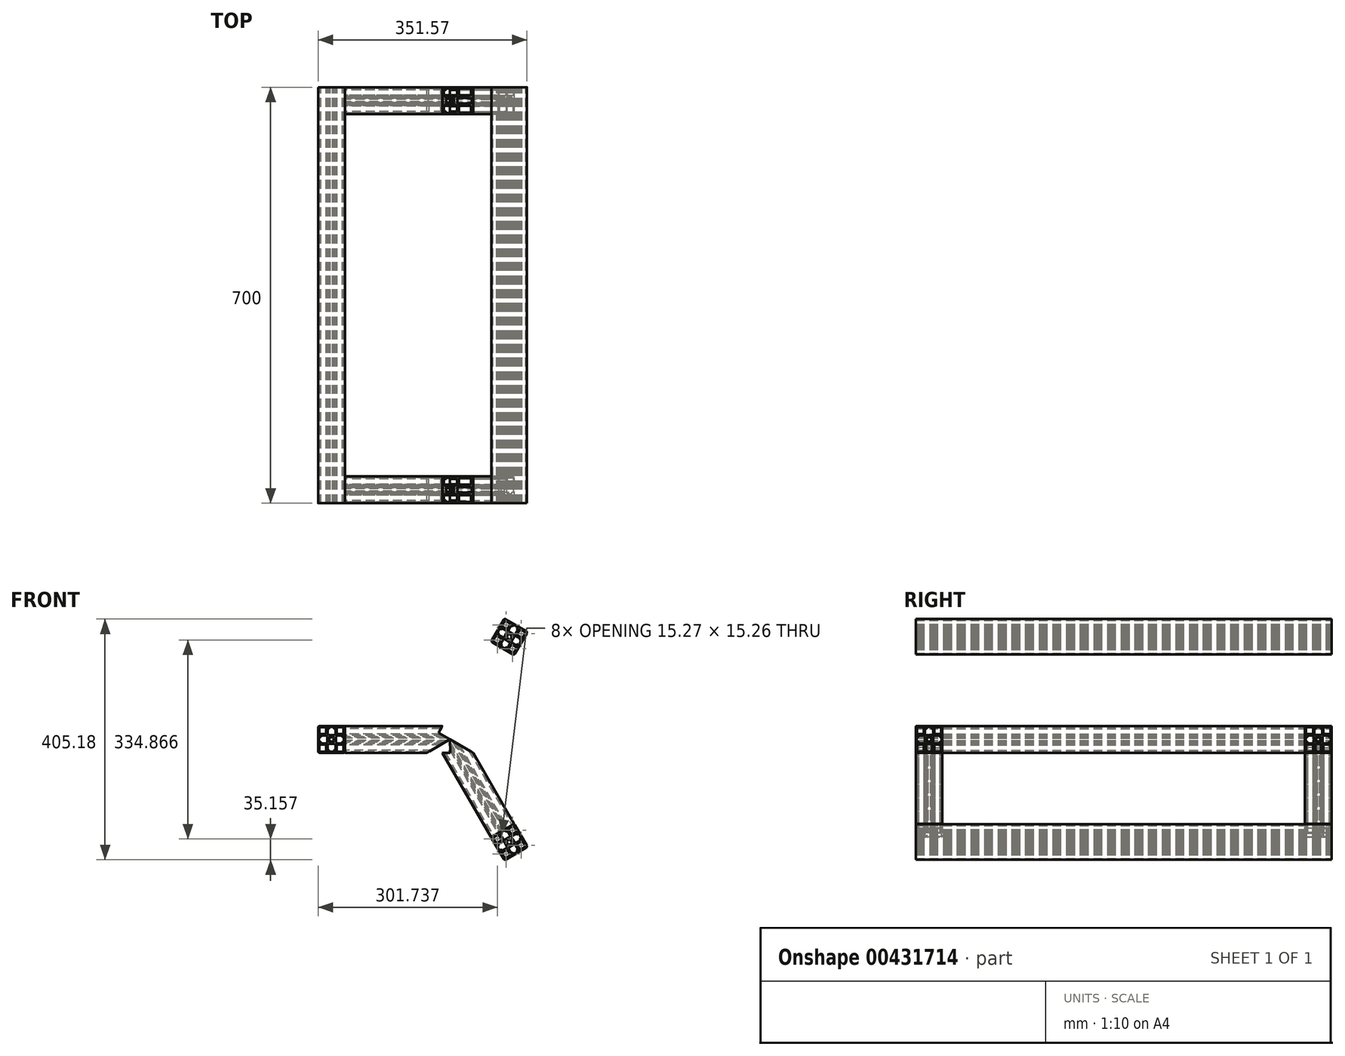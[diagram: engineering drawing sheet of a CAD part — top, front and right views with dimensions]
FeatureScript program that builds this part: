
annotation { "Feature Type Name" : "Feature", "Feature Type Description" : "" }
export const myFeature = defineFeature(function(context is Context, id is Id, definition is map)
    precondition{}
    {
        {
            var Q0;
            Q0=qCreatedBy(makeId("Front.planeOp"),FACE);
            var sketch = newSketch(context, id + "F0", { "sketchPlane" : qUnion([Q0])});
            skLineSegment(sketch, "E0", {"start": v(0, 22.5) * mm, "end": v(-20, 22.5) * mm});
            skLineSegment(sketch, "E1", {"start": v(-22.5, 20) * mm, "end": v(-22.5, 0) * mm});
            skLineSegment(sketch, "E2", {"start": v(0, 0) * mm, "end": v(-32.44, 0) * mm, "construction": true});
            skLineSegment(sketch, "E3", {"start": v(0, 0) * mm, "end": v(0, 27.63) * mm});
            skPoint(sketch, "E4.visualSharp", {"position": v(-22.5, 22.5) * mm});
            skArc(sketch, "E4.filletArc", {"start": v(-20, 22.5) * mm, "mid": v(-21.77, 21.77) * mm, "end": v(-22.5, 20) * mm});
            skLineSegment(sketch, "E5.bottom", {"start": v(-19.48, 8.8) * mm, "end": v(-9.78, 8.8) * mm});
            skLineSegment(sketch, "E5.top", {"start": v(-19.48, 20.52) * mm, "end": v(-9.78, 20.52) * mm});
            skLineSegment(sketch, "E5.left", {"start": v(-20.48, 9.8) * mm, "end": v(-20.48, 19.52) * mm});
            skLineSegment(sketch, "E5.right", {"start": v(-8.78, 9.8) * mm, "end": v(-8.78, 19.52) * mm});
            skLineSegment(sketch, "E6", {"start": v(-7.2, 0) * mm, "end": v(-7.2, 4.86) * mm});
            skLineSegment(sketch, "E7", {"start": v(-7.2, 4.86) * mm, "end": v(-9.19, 6.8) * mm});
            skLineSegment(sketch, "E8", {"start": v(-9.19, 6.8) * mm, "end": v(-18, 6.8) * mm});
            skLineSegment(sketch, "E9", {"start": v(-18, 6.8) * mm, "end": v(-18, 4.6) * mm});
            skLineSegment(sketch, "E10", {"start": v(-18.5, 4.1) * mm, "end": v(-22.2, 4.1) * mm});
            skLineSegment(sketch, "E11", {"start": v(-22.2, 4.1) * mm, "end": v(-22.2, 3.76) * mm});
            skLineSegment(sketch, "E12", {"start": v(-22.2, 3.76) * mm, "end": v(-21.67, 3.29) * mm});
            skLineSegment(sketch, "E13", {"start": v(-21, 1.8) * mm, "end": v(-21, 0) * mm});
            skLineSegment(sketch, "E14", {"start": v(0, 0) * mm, "end": v(-25.82, 25.82) * mm, "construction": true});
            skCircle(sketch, "E15", {"center": v(0, 0) * mm, "radius": 3.76 * mm});
            skLineSegment(sketch, "E16", {"start": v(-1.82, 3.3) * mm, "end": v(-3.13, 4.6) * mm});
            skLineSegment(sketch, "E17", {"start": v(-3.13, 4.6) * mm, "end": v(-3.86, 3.86) * mm});
            skPoint(sketch, "E18.visualSharp", {"position": v(-21, 2.7) * mm});
            skArc(sketch, "E18.filletArc", {"start": v(-21, 1.8) * mm, "mid": v(-21.17, 2.61) * mm, "end": v(-21.67, 3.29) * mm});
            skPoint(sketch, "E19.visualSharp", {"position": v(-18, 4.1) * mm});
            skArc(sketch, "E19.filletArc", {"start": v(-18.5, 4.1) * mm, "mid": v(-18.15, 4.24) * mm, "end": v(-18, 4.6) * mm});
            skPoint(sketch, "E20.visualSharp", {"position": v(-20.48, 20.52) * mm});
            skArc(sketch, "E20.filletArc", {"start": v(-19.48, 20.52) * mm, "mid": v(-20.19, 20.23) * mm, "end": v(-20.48, 19.52) * mm});
            skPoint(sketch, "E21.visualSharp", {"position": v(-20.48, 8.8) * mm});
            skArc(sketch, "E21.filletArc", {"start": v(-20.48, 9.8) * mm, "mid": v(-20.19, 9.1) * mm, "end": v(-19.48, 8.8) * mm});
            skPoint(sketch, "E22.visualSharp", {"position": v(-8.78, 8.8) * mm});
            skArc(sketch, "E22.filletArc", {"start": v(-9.78, 8.8) * mm, "mid": v(-9.07, 9.1) * mm, "end": v(-8.78, 9.8) * mm});
            skPoint(sketch, "E23.visualSharp", {"position": v(-8.78, 20.52) * mm});
            skArc(sketch, "E23.filletArc", {"start": v(-8.78, 19.52) * mm, "mid": v(-9.07, 20.23) * mm, "end": v(-9.78, 20.52) * mm});
            skLineSegment(sketch, "E24.MirrorCS", {"start": v(-4.86, 7.2) * mm, "end": v(-6.8, 9.19) * mm});
            skLineSegment(sketch, "E25.MirrorCS", {"start": v(0, 7.2) * mm, "end": v(-4.86, 7.2) * mm});
            skLineSegment(sketch, "E26.MirrorCS", {"start": v(-6.8, 9.19) * mm, "end": v(-6.8, 18) * mm});
            skLineSegment(sketch, "E27.MirrorCS", {"start": v(-6.8, 18) * mm, "end": v(-4.6, 18) * mm});
            skArc(sketch, "E28.MirrorCS", {"start": v(-4.1, 18.5) * mm, "mid": v(-4.24, 18.15) * mm, "end": v(-4.6, 18) * mm});
            skLineSegment(sketch, "E29.MirrorCS", {"start": v(-4.1, 18.5) * mm, "end": v(-4.1, 22.2) * mm});
            skLineSegment(sketch, "E30.MirrorCS", {"start": v(-1.8, 21) * mm, "end": v(0, 21) * mm});
            skArc(sketch, "E31.MirrorCS", {"start": v(-1.8, 21) * mm, "mid": v(-2.61, 21.17) * mm, "end": v(-3.29, 21.67) * mm});
            skLineSegment(sketch, "E32.MirrorCS", {"start": v(-3.76, 22.2) * mm, "end": v(-3.29, 21.67) * mm});
            skLineSegment(sketch, "E33.MirrorCS", {"start": v(-4.1, 22.2) * mm, "end": v(-3.76, 22.2) * mm});
            skLineSegment(sketch, "E34.MirrorCS", {"start": v(-3.3, 1.82) * mm, "end": v(-4.6, 3.13) * mm});
            skLineSegment(sketch, "E35.MirrorCS", {"start": v(-4.6, 3.13) * mm, "end": v(-3.86, 3.86) * mm});
            skLineSegment(sketch, "E36.MirrorCS", {"start": v(4.1, 22.2) * mm, "end": v(3.76, 22.2) * mm});
            skLineSegment(sketch, "E37.MirrorCS", {"start": v(3.76, 22.2) * mm, "end": v(3.29, 21.67) * mm});
            skLineSegment(sketch, "E38.MirrorCS", {"start": v(22.2, 3.76) * mm, "end": v(21.67, 3.29) * mm});
            skLineSegment(sketch, "E39.MirrorCS", {"start": v(22.2, 4.1) * mm, "end": v(22.2, 3.76) * mm});
            skArc(sketch, "E40.MirrorCS", {"start": v(4.1, 18.5) * mm, "mid": v(4.24, 18.15) * mm, "end": v(4.6, 18) * mm});
            skArc(sketch, "E41.MirrorCS", {"start": v(18.5, 4.1) * mm, "mid": v(18.15, 4.24) * mm, "end": v(18, 4.6) * mm});
            skArc(sketch, "E42.MirrorCS", {"start": v(19.48, 20.52) * mm, "mid": v(20.19, 20.23) * mm, "end": v(20.48, 19.52) * mm});
            skLineSegment(sketch, "E43.MirrorCS", {"start": v(3.13, 4.6) * mm, "end": v(3.86, 3.86) * mm});
            skLineSegment(sketch, "E44.MirrorCS", {"start": v(4.6, 3.13) * mm, "end": v(3.86, 3.86) * mm});
            skArc(sketch, "E45.MirrorCS", {"start": v(8.78, 19.52) * mm, "mid": v(9.07, 20.23) * mm, "end": v(9.78, 20.52) * mm});
            skArc(sketch, "E46.MirrorCS", {"start": v(9.78, 8.8) * mm, "mid": v(9.07, 9.1) * mm, "end": v(8.78, 9.8) * mm});
            skArc(sketch, "E47.MirrorCS", {"start": v(20.48, 9.8) * mm, "mid": v(20.19, 9.1) * mm, "end": v(19.48, 8.8) * mm});
            skArc(sketch, "E48.MirrorCS", {"start": v(21, 1.8) * mm, "mid": v(21.17, 2.61) * mm, "end": v(21.67, 3.29) * mm});
            skPoint(sketch, "E49.MirrorP", {"position": v(8.78, 8.8) * mm});
            skLineSegment(sketch, "E50.MirrorCS", {"start": v(4.86, 7.2) * mm, "end": v(6.8, 9.19) * mm});
            skLineSegment(sketch, "E51.MirrorCS", {"start": v(1.82, 3.3) * mm, "end": v(3.13, 4.6) * mm});
            skLineSegment(sketch, "E52.MirrorCS", {"start": v(6.8, 9.19) * mm, "end": v(6.8, 18) * mm});
            skLineSegment(sketch, "E53.MirrorCS", {"start": v(4.1, 18.5) * mm, "end": v(4.1, 22.2) * mm});
            skLineSegment(sketch, "E54.MirrorCS", {"start": v(21, 1.8) * mm, "end": v(21, 0) * mm});
            skPoint(sketch, "E55.MirrorP", {"position": v(20.48, 8.8) * mm});
            skPoint(sketch, "E56.MirrorP", {"position": v(20.48, 20.52) * mm});
            skPoint(sketch, "E57.MirrorP", {"position": v(8.78, 20.52) * mm});
            skLineSegment(sketch, "E58.MirrorCS", {"start": v(0, 0) * mm, "end": v(0, 27.63) * mm, "construction": true});
            skLineSegment(sketch, "E59.MirrorCS", {"start": v(22.5, 20) * mm, "end": v(22.5, 0) * mm});
            skLineSegment(sketch, "E60.MirrorCS", {"start": v(0, 22.5) * mm, "end": v(20, 22.5) * mm});
            skArc(sketch, "E61.MirrorCS", {"start": v(20, 22.5) * mm, "mid": v(21.77, 21.77) * mm, "end": v(22.5, 20) * mm});
            skLineSegment(sketch, "E62.MirrorCS", {"start": v(19.48, 8.8) * mm, "end": v(9.78, 8.8) * mm});
            skLineSegment(sketch, "E63.MirrorCS", {"start": v(19.48, 20.52) * mm, "end": v(9.78, 20.52) * mm});
            skLineSegment(sketch, "E64.MirrorCS", {"start": v(20.48, 9.8) * mm, "end": v(20.48, 19.52) * mm});
            skLineSegment(sketch, "E65.MirrorCS", {"start": v(8.78, 9.8) * mm, "end": v(8.78, 19.52) * mm});
            skLineSegment(sketch, "E66.MirrorCS", {"start": v(18.5, 4.1) * mm, "end": v(22.2, 4.1) * mm});
            skArc(sketch, "E67.MirrorCS", {"start": v(1.8, 21) * mm, "mid": v(2.61, 21.17) * mm, "end": v(3.29, 21.67) * mm});
            skLineSegment(sketch, "E68.MirrorCS", {"start": v(7.2, 0) * mm, "end": v(7.2, 4.86) * mm});
            skLineSegment(sketch, "E69.MirrorCS", {"start": v(7.2, 4.86) * mm, "end": v(9.19, 6.8) * mm});
            skPoint(sketch, "E70.MirrorP", {"position": v(21, 2.7) * mm});
            skLineSegment(sketch, "E71.MirrorCS", {"start": v(9.19, 6.8) * mm, "end": v(18, 6.8) * mm});
            skPoint(sketch, "E72.MirrorP", {"position": v(18, 4.1) * mm});
            skLineSegment(sketch, "E73.MirrorCS", {"start": v(3.3, 1.82) * mm, "end": v(4.6, 3.13) * mm});
            skLineSegment(sketch, "E74.MirrorCS", {"start": v(18, 6.8) * mm, "end": v(18, 4.6) * mm});
            skLineSegment(sketch, "E75.MirrorCS", {"start": v(1.8, 21) * mm, "end": v(0, 21) * mm});
            skLineSegment(sketch, "E76.MirrorCS", {"start": v(0, 7.2) * mm, "end": v(4.86, 7.2) * mm});
            skLineSegment(sketch, "E77.MirrorCS", {"start": v(6.8, 18) * mm, "end": v(4.6, 18) * mm});
            skPoint(sketch, "E78.MirrorP", {"position": v(22.5, 22.5) * mm});
            skArc(sketch, "E79.MirrorCS", {"start": v(18.5, -4.1) * mm, "mid": v(18.15, -4.24) * mm, "end": v(18, -4.6) * mm});
            skArc(sketch, "E80.MirrorCS", {"start": v(-18.5, -4.1) * mm, "mid": v(-18.15, -4.24) * mm, "end": v(-18, -4.6) * mm});
            skLineSegment(sketch, "E81.MirrorCS", {"start": v(-3.76, -22.2) * mm, "end": v(-3.29, -21.67) * mm});
            skLineSegment(sketch, "E82.MirrorCS", {"start": v(22.2, -4.1) * mm, "end": v(22.2, -3.76) * mm});
            skLineSegment(sketch, "E83.MirrorCS", {"start": v(22.2, -3.76) * mm, "end": v(21.67, -3.29) * mm});
            skLineSegment(sketch, "E84.MirrorCS", {"start": v(-22.2, -3.76) * mm, "end": v(-21.67, -3.29) * mm});
            skLineSegment(sketch, "E85.MirrorCS", {"start": v(-22.2, -4.1) * mm, "end": v(-22.2, -3.76) * mm});
            skArc(sketch, "E86.MirrorCS", {"start": v(4.1, -18.5) * mm, "mid": v(4.24, -18.15) * mm, "end": v(4.6, -18) * mm});
            skLineSegment(sketch, "E87.MirrorCS", {"start": v(4.1, -22.2) * mm, "end": v(3.76, -22.2) * mm});
            skLineSegment(sketch, "E88.MirrorCS", {"start": v(-4.1, -22.2) * mm, "end": v(-3.76, -22.2) * mm});
            skLineSegment(sketch, "E89.MirrorCS", {"start": v(3.76, -22.2) * mm, "end": v(3.29, -21.67) * mm});
            skArc(sketch, "E90.MirrorCS", {"start": v(-4.1, -18.5) * mm, "mid": v(-4.24, -18.15) * mm, "end": v(-4.6, -18) * mm});
            skArc(sketch, "E91.MirrorCS", {"start": v(-19.48, -20.52) * mm, "mid": v(-20.19, -20.23) * mm, "end": v(-20.48, -19.52) * mm});
            skArc(sketch, "E92.MirrorCS", {"start": v(19.48, -20.52) * mm, "mid": v(20.19, -20.23) * mm, "end": v(20.48, -19.52) * mm});
            skLineSegment(sketch, "E93.MirrorCS", {"start": v(3.13, -4.6) * mm, "end": v(3.86, -3.86) * mm});
            skArc(sketch, "E94.MirrorCS", {"start": v(21, -1.8) * mm, "mid": v(21.17, -2.61) * mm, "end": v(21.67, -3.29) * mm});
            skLineSegment(sketch, "E95.MirrorCS", {"start": v(-1.82, -3.3) * mm, "end": v(-3.13, -4.6) * mm});
            skArc(sketch, "E96.MirrorCS", {"start": v(-8.78, -19.52) * mm, "mid": v(-9.07, -20.23) * mm, "end": v(-9.78, -20.52) * mm});
            skArc(sketch, "E97.MirrorCS", {"start": v(20.48, -9.8) * mm, "mid": v(20.19, -9.1) * mm, "end": v(19.48, -8.8) * mm});
            skArc(sketch, "E98.MirrorCS", {"start": v(1.8, -21) * mm, "mid": v(2.61, -21.17) * mm, "end": v(3.29, -21.67) * mm});
            skArc(sketch, "E99.MirrorCS", {"start": v(-1.8, -21) * mm, "mid": v(-2.61, -21.17) * mm, "end": v(-3.29, -21.67) * mm});
            skArc(sketch, "E100.MirrorCS", {"start": v(-9.78, -8.8) * mm, "mid": v(-9.07, -9.1) * mm, "end": v(-8.78, -9.8) * mm});
            skArc(sketch, "E101.MirrorCS", {"start": v(9.78, -8.8) * mm, "mid": v(9.07, -9.1) * mm, "end": v(8.78, -9.8) * mm});
            skLineSegment(sketch, "E102.MirrorCS", {"start": v(-3.13, -4.6) * mm, "end": v(-3.86, -3.86) * mm});
            skArc(sketch, "E103.MirrorCS", {"start": v(8.78, -19.52) * mm, "mid": v(9.07, -20.23) * mm, "end": v(9.78, -20.52) * mm});
            skLineSegment(sketch, "E104.MirrorCS", {"start": v(-1.8, -21) * mm, "end": v(0, -21) * mm});
            skArc(sketch, "E105.MirrorCS", {"start": v(-20.48, -9.8) * mm, "mid": v(-20.19, -9.1) * mm, "end": v(-19.48, -8.8) * mm});
            skLineSegment(sketch, "E106.MirrorCS", {"start": v(1.82, -3.3) * mm, "end": v(3.13, -4.6) * mm});
            skArc(sketch, "E107.MirrorCS", {"start": v(-21, -1.8) * mm, "mid": v(-21.17, -2.61) * mm, "end": v(-21.67, -3.29) * mm});
            skLineSegment(sketch, "E108.MirrorCS", {"start": v(-3.3, -1.82) * mm, "end": v(-4.6, -3.13) * mm});
            skLineSegment(sketch, "E109.MirrorCS", {"start": v(1.8, -21) * mm, "end": v(0, -21) * mm});
            skLineSegment(sketch, "E110.MirrorCS", {"start": v(4.6, -3.13) * mm, "end": v(3.86, -3.86) * mm});
            skLineSegment(sketch, "E111.MirrorCS", {"start": v(-4.6, -3.13) * mm, "end": v(-3.86, -3.86) * mm});
            skLineSegment(sketch, "E112.MirrorCS", {"start": v(21, -1.8) * mm, "end": v(21, 0) * mm});
            skLineSegment(sketch, "E113.MirrorCS", {"start": v(3.3, -1.82) * mm, "end": v(4.6, -3.13) * mm});
            skLineSegment(sketch, "E114.MirrorCS", {"start": v(-21, -1.8) * mm, "end": v(-21, 0) * mm});
            skPoint(sketch, "E115.MirrorP", {"position": v(-20.48, -8.8) * mm});
            skPoint(sketch, "E116.MirrorP", {"position": v(22.5, -22.5) * mm});
            skPoint(sketch, "E117.MirrorP", {"position": v(20.48, -8.8) * mm});
            skPoint(sketch, "E118.MirrorP", {"position": v(-22.5, -22.5) * mm});
            skLineSegment(sketch, "E119.MirrorCS", {"start": v(7.2, 0) * mm, "end": v(7.2, -4.86) * mm});
            skLineSegment(sketch, "E120.MirrorCS", {"start": v(22.5, -20) * mm, "end": v(22.5, 0) * mm});
            skLineSegment(sketch, "E121.MirrorCS", {"start": v(6.8, -18) * mm, "end": v(4.6, -18) * mm});
            skPoint(sketch, "E122.MirrorP", {"position": v(18, -4.1) * mm});
            skPoint(sketch, "E123.MirrorP", {"position": v(-18, -4.1) * mm});
            skPoint(sketch, "E124.MirrorP", {"position": v(21, -2.7) * mm});
            skLineSegment(sketch, "E125.MirrorCS", {"start": v(-18, -6.8) * mm, "end": v(-18, -4.6) * mm});
            skLineSegment(sketch, "E126.MirrorCS", {"start": v(-9.19, -6.8) * mm, "end": v(-18, -6.8) * mm});
            skLineSegment(sketch, "E127.MirrorCS", {"start": v(0, -7.2) * mm, "end": v(4.86, -7.2) * mm});
            skLineSegment(sketch, "E128.MirrorCS", {"start": v(-7.2, -4.86) * mm, "end": v(-9.19, -6.8) * mm});
            skLineSegment(sketch, "E129.MirrorCS", {"start": v(-7.2, 0) * mm, "end": v(-7.2, -4.86) * mm});
            skLineSegment(sketch, "E130.MirrorCS", {"start": v(-8.78, -9.8) * mm, "end": v(-8.78, -19.52) * mm});
            skLineSegment(sketch, "E131.MirrorCS", {"start": v(-20.48, -9.8) * mm, "end": v(-20.48, -19.52) * mm});
            skLineSegment(sketch, "E132.MirrorCS", {"start": v(-19.48, -20.52) * mm, "end": v(-9.78, -20.52) * mm});
            skLineSegment(sketch, "E133.MirrorCS", {"start": v(-19.48, -8.8) * mm, "end": v(-9.78, -8.8) * mm});
            skArc(sketch, "E134.MirrorCS", {"start": v(-20, -22.5) * mm, "mid": v(-21.77, -21.77) * mm, "end": v(-22.5, -20) * mm});
            skLineSegment(sketch, "E135.MirrorCS", {"start": v(-22.5, -20) * mm, "end": v(-22.5, 0) * mm});
            skLineSegment(sketch, "E136.MirrorCS", {"start": v(0, -22.5) * mm, "end": v(-20, -22.5) * mm});
            skLineSegment(sketch, "E137.MirrorCS", {"start": v(-18.5, -4.1) * mm, "end": v(-22.2, -4.1) * mm});
            skLineSegment(sketch, "E138.MirrorCS", {"start": v(18.5, -4.1) * mm, "end": v(22.2, -4.1) * mm});
            skLineSegment(sketch, "E139.MirrorCS", {"start": v(0, -22.5) * mm, "end": v(20, -22.5) * mm});
            skLineSegment(sketch, "E140.MirrorCS", {"start": v(4.1, -18.5) * mm, "end": v(4.1, -22.2) * mm});
            skLineSegment(sketch, "E141.MirrorCS", {"start": v(-4.86, -7.2) * mm, "end": v(-6.8, -9.19) * mm});
            skLineSegment(sketch, "E142.MirrorCS", {"start": v(-6.8, -9.19) * mm, "end": v(-6.8, -18) * mm});
            skLineSegment(sketch, "E143.MirrorCS", {"start": v(18, -6.8) * mm, "end": v(18, -4.6) * mm});
            skPoint(sketch, "E144.MirrorP", {"position": v(-21, -2.7) * mm});
            skLineSegment(sketch, "E145.MirrorCS", {"start": v(19.48, -8.8) * mm, "end": v(9.78, -8.8) * mm});
            skLineSegment(sketch, "E146.MirrorCS", {"start": v(7.2, -4.86) * mm, "end": v(9.19, -6.8) * mm});
            skPoint(sketch, "E147.MirrorP", {"position": v(-8.78, -20.52) * mm});
            skLineSegment(sketch, "E148.MirrorCS", {"start": v(4.86, -7.2) * mm, "end": v(6.8, -9.19) * mm});
            skPoint(sketch, "E149.MirrorP", {"position": v(-20.48, -20.52) * mm});
            skLineSegment(sketch, "E150.MirrorCS", {"start": v(8.78, -9.8) * mm, "end": v(8.78, -19.52) * mm});
            skPoint(sketch, "E151.MirrorP", {"position": v(8.78, -8.8) * mm});
            skLineSegment(sketch, "E152.MirrorCS", {"start": v(19.48, -20.52) * mm, "end": v(9.78, -20.52) * mm});
            skLineSegment(sketch, "E153.MirrorCS", {"start": v(9.19, -6.8) * mm, "end": v(18, -6.8) * mm});
            skLineSegment(sketch, "E154.MirrorCS", {"start": v(-6.8, -18) * mm, "end": v(-4.6, -18) * mm});
            skLineSegment(sketch, "E155.MirrorCS", {"start": v(0, -7.2) * mm, "end": v(-4.86, -7.2) * mm});
            skLineSegment(sketch, "E156.MirrorCS", {"start": v(-4.1, -18.5) * mm, "end": v(-4.1, -22.2) * mm});
            skPoint(sketch, "E157.MirrorP", {"position": v(8.78, -20.52) * mm});
            skArc(sketch, "E158.MirrorCS", {"start": v(20, -22.5) * mm, "mid": v(21.77, -21.77) * mm, "end": v(22.5, -20) * mm});
            skPoint(sketch, "E159.MirrorP", {"position": v(-8.78, -8.8) * mm});
            skPoint(sketch, "E160.MirrorP", {"position": v(20.48, -20.52) * mm});
            skLineSegment(sketch, "E161.MirrorCS", {"start": v(6.8, -9.19) * mm, "end": v(6.8, -18) * mm});
            skLineSegment(sketch, "E162.MirrorCS", {"start": v(20.48, -9.8) * mm, "end": v(20.48, -19.52) * mm});
            skSolve(sketch);
        }
        {
            var Q0;
            Q0=makeQuery(id+"F0.imprint","IMPRINT",FACE,{"disambiguationData":[TD([[makeQuery(id+"F0.imprint","IMPRINT",EDGE,{"derivedFrom":sQuery(id+"F0.wireOp",EDGE,"E0")}),1.0]])]});
            extrude(context, id + "F1", {"entities" : qUnion([Q0]), "depth" : 700 * mm});
        }
        {
            var Q0;
            Q0=makeQuery(id+"F1.opExtrude","SWEPT_BODY",BODY,{"disambiguationData":[OSD([sQuery(id+"F0.wireOp",EDGE,"E0"),sQuery(id+"F0.wireOp",EDGE,"E1"),sQuery(id+"F0.wireOp",EDGE,"E4.filletArc"),sQuery(id+"F0.wireOp",EDGE,"E5.bottom"),sQuery(id+"F0.wireOp",EDGE,"E5.top"),sQuery(id+"F0.wireOp",EDGE,"E5.left"),sQuery(id+"F0.wireOp",EDGE,"E5.right"),sQuery(id+"F0.wireOp",EDGE,"E6"),sQuery(id+"F0.wireOp",EDGE,"E7"),sQuery(id+"F0.wireOp",EDGE,"E8"),sQuery(id+"F0.wireOp",EDGE,"E9"),sQuery(id+"F0.wireOp",EDGE,"E10"),sQuery(id+"F0.wireOp",EDGE,"E11"),sQuery(id+"F0.wireOp",EDGE,"E12"),sQuery(id+"F0.wireOp",EDGE,"E13"),sQuery(id+"F0.wireOp",EDGE,"E15"),sQuery(id+"F0.wireOp",EDGE,"E16"),sQuery(id+"F0.wireOp",EDGE,"E17"),sQuery(id+"F0.wireOp",EDGE,"E18.filletArc"),sQuery(id+"F0.wireOp",EDGE,"E19.filletArc"),sQuery(id+"F0.wireOp",EDGE,"E20.filletArc"),sQuery(id+"F0.wireOp",EDGE,"E21.filletArc"),sQuery(id+"F0.wireOp",EDGE,"E22.filletArc"),sQuery(id+"F0.wireOp",EDGE,"E23.filletArc"),sQuery(id+"F0.wireOp",EDGE,"E24.MirrorCS"),sQuery(id+"F0.wireOp",EDGE,"E25.MirrorCS"),sQuery(id+"F0.wireOp",EDGE,"E26.MirrorCS"),sQuery(id+"F0.wireOp",EDGE,"E27.MirrorCS"),sQuery(id+"F0.wireOp",EDGE,"E28.MirrorCS"),sQuery(id+"F0.wireOp",EDGE,"E29.MirrorCS"),sQuery(id+"F0.wireOp",EDGE,"E30.MirrorCS"),sQuery(id+"F0.wireOp",EDGE,"E31.MirrorCS"),sQuery(id+"F0.wireOp",EDGE,"E32.MirrorCS"),sQuery(id+"F0.wireOp",EDGE,"E33.MirrorCS"),sQuery(id+"F0.wireOp",EDGE,"E34.MirrorCS"),sQuery(id+"F0.wireOp",EDGE,"E35.MirrorCS"),sQuery(id+"F0.wireOp",EDGE,"E36.MirrorCS"),sQuery(id+"F0.wireOp",EDGE,"E37.MirrorCS"),sQuery(id+"F0.wireOp",EDGE,"E38.MirrorCS"),sQuery(id+"F0.wireOp",EDGE,"E39.MirrorCS"),sQuery(id+"F0.wireOp",EDGE,"E40.MirrorCS"),sQuery(id+"F0.wireOp",EDGE,"E41.MirrorCS"),sQuery(id+"F0.wireOp",EDGE,"E42.MirrorCS"),sQuery(id+"F0.wireOp",EDGE,"E43.MirrorCS"),sQuery(id+"F0.wireOp",EDGE,"E44.MirrorCS"),sQuery(id+"F0.wireOp",EDGE,"E45.MirrorCS"),sQuery(id+"F0.wireOp",EDGE,"E46.MirrorCS"),sQuery(id+"F0.wireOp",EDGE,"E47.MirrorCS"),sQuery(id+"F0.wireOp",EDGE,"E48.MirrorCS"),sQuery(id+"F0.wireOp",EDGE,"E50.MirrorCS"),sQuery(id+"F0.wireOp",EDGE,"E51.MirrorCS"),sQuery(id+"F0.wireOp",EDGE,"E52.MirrorCS"),sQuery(id+"F0.wireOp",EDGE,"E53.MirrorCS"),sQuery(id+"F0.wireOp",EDGE,"E54.MirrorCS"),sQuery(id+"F0.wireOp",EDGE,"E59.MirrorCS"),sQuery(id+"F0.wireOp",EDGE,"E60.MirrorCS"),sQuery(id+"F0.wireOp",EDGE,"E61.MirrorCS"),sQuery(id+"F0.wireOp",EDGE,"E62.MirrorCS"),sQuery(id+"F0.wireOp",EDGE,"E63.MirrorCS"),sQuery(id+"F0.wireOp",EDGE,"E64.MirrorCS"),sQuery(id+"F0.wireOp",EDGE,"E65.MirrorCS"),sQuery(id+"F0.wireOp",EDGE,"E66.MirrorCS"),sQuery(id+"F0.wireOp",EDGE,"E67.MirrorCS"),sQuery(id+"F0.wireOp",EDGE,"E68.MirrorCS"),sQuery(id+"F0.wireOp",EDGE,"E69.MirrorCS"),sQuery(id+"F0.wireOp",EDGE,"E71.MirrorCS"),sQuery(id+"F0.wireOp",EDGE,"E73.MirrorCS"),sQuery(id+"F0.wireOp",EDGE,"E74.MirrorCS"),sQuery(id+"F0.wireOp",EDGE,"E75.MirrorCS"),sQuery(id+"F0.wireOp",EDGE,"E76.MirrorCS"),sQuery(id+"F0.wireOp",EDGE,"E77.MirrorCS"),sQuery(id+"F0.wireOp",EDGE,"E79.MirrorCS"),sQuery(id+"F0.wireOp",EDGE,"E80.MirrorCS"),sQuery(id+"F0.wireOp",EDGE,"E81.MirrorCS"),sQuery(id+"F0.wireOp",EDGE,"E82.MirrorCS"),sQuery(id+"F0.wireOp",EDGE,"E83.MirrorCS"),sQuery(id+"F0.wireOp",EDGE,"E84.MirrorCS"),sQuery(id+"F0.wireOp",EDGE,"E85.MirrorCS"),sQuery(id+"F0.wireOp",EDGE,"E86.MirrorCS"),sQuery(id+"F0.wireOp",EDGE,"E87.MirrorCS"),sQuery(id+"F0.wireOp",EDGE,"E88.MirrorCS"),sQuery(id+"F0.wireOp",EDGE,"E89.MirrorCS"),sQuery(id+"F0.wireOp",EDGE,"E90.MirrorCS"),sQuery(id+"F0.wireOp",EDGE,"E91.MirrorCS"),sQuery(id+"F0.wireOp",EDGE,"E92.MirrorCS"),sQuery(id+"F0.wireOp",EDGE,"E93.MirrorCS"),sQuery(id+"F0.wireOp",EDGE,"E94.MirrorCS"),sQuery(id+"F0.wireOp",EDGE,"E95.MirrorCS"),sQuery(id+"F0.wireOp",EDGE,"E96.MirrorCS"),sQuery(id+"F0.wireOp",EDGE,"E97.MirrorCS"),sQuery(id+"F0.wireOp",EDGE,"E98.MirrorCS"),sQuery(id+"F0.wireOp",EDGE,"E99.MirrorCS"),sQuery(id+"F0.wireOp",EDGE,"E100.MirrorCS"),sQuery(id+"F0.wireOp",EDGE,"E101.MirrorCS"),sQuery(id+"F0.wireOp",EDGE,"E102.MirrorCS"),sQuery(id+"F0.wireOp",EDGE,"E103.MirrorCS"),sQuery(id+"F0.wireOp",EDGE,"E104.MirrorCS"),sQuery(id+"F0.wireOp",EDGE,"E105.MirrorCS"),sQuery(id+"F0.wireOp",EDGE,"E106.MirrorCS"),sQuery(id+"F0.wireOp",EDGE,"E107.MirrorCS"),sQuery(id+"F0.wireOp",EDGE,"E108.MirrorCS"),sQuery(id+"F0.wireOp",EDGE,"E109.MirrorCS"),sQuery(id+"F0.wireOp",EDGE,"E110.MirrorCS"),sQuery(id+"F0.wireOp",EDGE,"E111.MirrorCS"),sQuery(id+"F0.wireOp",EDGE,"E112.MirrorCS"),sQuery(id+"F0.wireOp",EDGE,"E113.MirrorCS"),sQuery(id+"F0.wireOp",EDGE,"E114.MirrorCS"),sQuery(id+"F0.wireOp",EDGE,"E119.MirrorCS"),sQuery(id+"F0.wireOp",EDGE,"E120.MirrorCS"),sQuery(id+"F0.wireOp",EDGE,"E121.MirrorCS"),sQuery(id+"F0.wireOp",EDGE,"E125.MirrorCS"),sQuery(id+"F0.wireOp",EDGE,"E126.MirrorCS"),sQuery(id+"F0.wireOp",EDGE,"E127.MirrorCS"),sQuery(id+"F0.wireOp",EDGE,"E128.MirrorCS"),sQuery(id+"F0.wireOp",EDGE,"E129.MirrorCS"),sQuery(id+"F0.wireOp",EDGE,"E130.MirrorCS"),sQuery(id+"F0.wireOp",EDGE,"E131.MirrorCS"),sQuery(id+"F0.wireOp",EDGE,"E132.MirrorCS"),sQuery(id+"F0.wireOp",EDGE,"E133.MirrorCS"),sQuery(id+"F0.wireOp",EDGE,"E134.MirrorCS"),sQuery(id+"F0.wireOp",EDGE,"E135.MirrorCS"),sQuery(id+"F0.wireOp",EDGE,"E136.MirrorCS"),sQuery(id+"F0.wireOp",EDGE,"E137.MirrorCS"),sQuery(id+"F0.wireOp",EDGE,"E138.MirrorCS"),sQuery(id+"F0.wireOp",EDGE,"E139.MirrorCS"),sQuery(id+"F0.wireOp",EDGE,"E140.MirrorCS"),sQuery(id+"F0.wireOp",EDGE,"E141.MirrorCS"),sQuery(id+"F0.wireOp",EDGE,"E142.MirrorCS"),sQuery(id+"F0.wireOp",EDGE,"E143.MirrorCS"),sQuery(id+"F0.wireOp",EDGE,"E145.MirrorCS"),sQuery(id+"F0.wireOp",EDGE,"E146.MirrorCS"),sQuery(id+"F0.wireOp",EDGE,"E148.MirrorCS"),sQuery(id+"F0.wireOp",EDGE,"E150.MirrorCS"),sQuery(id+"F0.wireOp",EDGE,"E152.MirrorCS"),sQuery(id+"F0.wireOp",EDGE,"E153.MirrorCS"),sQuery(id+"F0.wireOp",EDGE,"E154.MirrorCS"),sQuery(id+"F0.wireOp",EDGE,"E155.MirrorCS"),sQuery(id+"F0.wireOp",EDGE,"E156.MirrorCS"),sQuery(id+"F0.wireOp",EDGE,"E158.MirrorCS"),sQuery(id+"F0.wireOp",EDGE,"E161.MirrorCS"),sQuery(id+"F0.wireOp",EDGE,"E162.MirrorCS")])]});
            transform(context, id + "F2", {"entities" : qUnion([Q0]), "transformType" : TransformType.TRANSLATION_3D, "dx" : -199.5 * mm, "dy" : 0 * mm, "dz" : 0 * mm, "makeCopy" : false});
        }
        {
            var Q0;
            Q0=makeQuery(id+"F1.opExtrude","SWEPT_BODY",BODY,{"disambiguationData":[OSD([sQuery(id+"F0.wireOp",EDGE,"E0"),sQuery(id+"F0.wireOp",EDGE,"E1"),sQuery(id+"F0.wireOp",EDGE,"E4.filletArc"),sQuery(id+"F0.wireOp",EDGE,"E5.bottom"),sQuery(id+"F0.wireOp",EDGE,"E5.top"),sQuery(id+"F0.wireOp",EDGE,"E5.left"),sQuery(id+"F0.wireOp",EDGE,"E5.right"),sQuery(id+"F0.wireOp",EDGE,"E6"),sQuery(id+"F0.wireOp",EDGE,"E7"),sQuery(id+"F0.wireOp",EDGE,"E8"),sQuery(id+"F0.wireOp",EDGE,"E9"),sQuery(id+"F0.wireOp",EDGE,"E10"),sQuery(id+"F0.wireOp",EDGE,"E11"),sQuery(id+"F0.wireOp",EDGE,"E12"),sQuery(id+"F0.wireOp",EDGE,"E13"),sQuery(id+"F0.wireOp",EDGE,"E15"),sQuery(id+"F0.wireOp",EDGE,"E16"),sQuery(id+"F0.wireOp",EDGE,"E17"),sQuery(id+"F0.wireOp",EDGE,"E18.filletArc"),sQuery(id+"F0.wireOp",EDGE,"E19.filletArc"),sQuery(id+"F0.wireOp",EDGE,"E20.filletArc"),sQuery(id+"F0.wireOp",EDGE,"E21.filletArc"),sQuery(id+"F0.wireOp",EDGE,"E22.filletArc"),sQuery(id+"F0.wireOp",EDGE,"E23.filletArc"),sQuery(id+"F0.wireOp",EDGE,"E24.MirrorCS"),sQuery(id+"F0.wireOp",EDGE,"E25.MirrorCS"),sQuery(id+"F0.wireOp",EDGE,"E26.MirrorCS"),sQuery(id+"F0.wireOp",EDGE,"E27.MirrorCS"),sQuery(id+"F0.wireOp",EDGE,"E28.MirrorCS"),sQuery(id+"F0.wireOp",EDGE,"E29.MirrorCS"),sQuery(id+"F0.wireOp",EDGE,"E30.MirrorCS"),sQuery(id+"F0.wireOp",EDGE,"E31.MirrorCS"),sQuery(id+"F0.wireOp",EDGE,"E32.MirrorCS"),sQuery(id+"F0.wireOp",EDGE,"E33.MirrorCS"),sQuery(id+"F0.wireOp",EDGE,"E34.MirrorCS"),sQuery(id+"F0.wireOp",EDGE,"E35.MirrorCS"),sQuery(id+"F0.wireOp",EDGE,"E36.MirrorCS"),sQuery(id+"F0.wireOp",EDGE,"E37.MirrorCS"),sQuery(id+"F0.wireOp",EDGE,"E38.MirrorCS"),sQuery(id+"F0.wireOp",EDGE,"E39.MirrorCS"),sQuery(id+"F0.wireOp",EDGE,"E40.MirrorCS"),sQuery(id+"F0.wireOp",EDGE,"E41.MirrorCS"),sQuery(id+"F0.wireOp",EDGE,"E42.MirrorCS"),sQuery(id+"F0.wireOp",EDGE,"E43.MirrorCS"),sQuery(id+"F0.wireOp",EDGE,"E44.MirrorCS"),sQuery(id+"F0.wireOp",EDGE,"E45.MirrorCS"),sQuery(id+"F0.wireOp",EDGE,"E46.MirrorCS"),sQuery(id+"F0.wireOp",EDGE,"E47.MirrorCS"),sQuery(id+"F0.wireOp",EDGE,"E48.MirrorCS"),sQuery(id+"F0.wireOp",EDGE,"E50.MirrorCS"),sQuery(id+"F0.wireOp",EDGE,"E51.MirrorCS"),sQuery(id+"F0.wireOp",EDGE,"E52.MirrorCS"),sQuery(id+"F0.wireOp",EDGE,"E53.MirrorCS"),sQuery(id+"F0.wireOp",EDGE,"E54.MirrorCS"),sQuery(id+"F0.wireOp",EDGE,"E59.MirrorCS"),sQuery(id+"F0.wireOp",EDGE,"E60.MirrorCS"),sQuery(id+"F0.wireOp",EDGE,"E61.MirrorCS"),sQuery(id+"F0.wireOp",EDGE,"E62.MirrorCS"),sQuery(id+"F0.wireOp",EDGE,"E63.MirrorCS"),sQuery(id+"F0.wireOp",EDGE,"E64.MirrorCS"),sQuery(id+"F0.wireOp",EDGE,"E65.MirrorCS"),sQuery(id+"F0.wireOp",EDGE,"E66.MirrorCS"),sQuery(id+"F0.wireOp",EDGE,"E67.MirrorCS"),sQuery(id+"F0.wireOp",EDGE,"E68.MirrorCS"),sQuery(id+"F0.wireOp",EDGE,"E69.MirrorCS"),sQuery(id+"F0.wireOp",EDGE,"E71.MirrorCS"),sQuery(id+"F0.wireOp",EDGE,"E73.MirrorCS"),sQuery(id+"F0.wireOp",EDGE,"E74.MirrorCS"),sQuery(id+"F0.wireOp",EDGE,"E75.MirrorCS"),sQuery(id+"F0.wireOp",EDGE,"E76.MirrorCS"),sQuery(id+"F0.wireOp",EDGE,"E77.MirrorCS"),sQuery(id+"F0.wireOp",EDGE,"E79.MirrorCS"),sQuery(id+"F0.wireOp",EDGE,"E80.MirrorCS"),sQuery(id+"F0.wireOp",EDGE,"E81.MirrorCS"),sQuery(id+"F0.wireOp",EDGE,"E82.MirrorCS"),sQuery(id+"F0.wireOp",EDGE,"E83.MirrorCS"),sQuery(id+"F0.wireOp",EDGE,"E84.MirrorCS"),sQuery(id+"F0.wireOp",EDGE,"E85.MirrorCS"),sQuery(id+"F0.wireOp",EDGE,"E86.MirrorCS"),sQuery(id+"F0.wireOp",EDGE,"E87.MirrorCS"),sQuery(id+"F0.wireOp",EDGE,"E88.MirrorCS"),sQuery(id+"F0.wireOp",EDGE,"E89.MirrorCS"),sQuery(id+"F0.wireOp",EDGE,"E90.MirrorCS"),sQuery(id+"F0.wireOp",EDGE,"E91.MirrorCS"),sQuery(id+"F0.wireOp",EDGE,"E92.MirrorCS"),sQuery(id+"F0.wireOp",EDGE,"E93.MirrorCS"),sQuery(id+"F0.wireOp",EDGE,"E94.MirrorCS"),sQuery(id+"F0.wireOp",EDGE,"E95.MirrorCS"),sQuery(id+"F0.wireOp",EDGE,"E96.MirrorCS"),sQuery(id+"F0.wireOp",EDGE,"E97.MirrorCS"),sQuery(id+"F0.wireOp",EDGE,"E98.MirrorCS"),sQuery(id+"F0.wireOp",EDGE,"E99.MirrorCS"),sQuery(id+"F0.wireOp",EDGE,"E100.MirrorCS"),sQuery(id+"F0.wireOp",EDGE,"E101.MirrorCS"),sQuery(id+"F0.wireOp",EDGE,"E102.MirrorCS"),sQuery(id+"F0.wireOp",EDGE,"E103.MirrorCS"),sQuery(id+"F0.wireOp",EDGE,"E104.MirrorCS"),sQuery(id+"F0.wireOp",EDGE,"E105.MirrorCS"),sQuery(id+"F0.wireOp",EDGE,"E106.MirrorCS"),sQuery(id+"F0.wireOp",EDGE,"E107.MirrorCS"),sQuery(id+"F0.wireOp",EDGE,"E108.MirrorCS"),sQuery(id+"F0.wireOp",EDGE,"E109.MirrorCS"),sQuery(id+"F0.wireOp",EDGE,"E110.MirrorCS"),sQuery(id+"F0.wireOp",EDGE,"E111.MirrorCS"),sQuery(id+"F0.wireOp",EDGE,"E112.MirrorCS"),sQuery(id+"F0.wireOp",EDGE,"E113.MirrorCS"),sQuery(id+"F0.wireOp",EDGE,"E114.MirrorCS"),sQuery(id+"F0.wireOp",EDGE,"E119.MirrorCS"),sQuery(id+"F0.wireOp",EDGE,"E120.MirrorCS"),sQuery(id+"F0.wireOp",EDGE,"E121.MirrorCS"),sQuery(id+"F0.wireOp",EDGE,"E125.MirrorCS"),sQuery(id+"F0.wireOp",EDGE,"E126.MirrorCS"),sQuery(id+"F0.wireOp",EDGE,"E127.MirrorCS"),sQuery(id+"F0.wireOp",EDGE,"E128.MirrorCS"),sQuery(id+"F0.wireOp",EDGE,"E129.MirrorCS"),sQuery(id+"F0.wireOp",EDGE,"E130.MirrorCS"),sQuery(id+"F0.wireOp",EDGE,"E131.MirrorCS"),sQuery(id+"F0.wireOp",EDGE,"E132.MirrorCS"),sQuery(id+"F0.wireOp",EDGE,"E133.MirrorCS"),sQuery(id+"F0.wireOp",EDGE,"E134.MirrorCS"),sQuery(id+"F0.wireOp",EDGE,"E135.MirrorCS"),sQuery(id+"F0.wireOp",EDGE,"E136.MirrorCS"),sQuery(id+"F0.wireOp",EDGE,"E137.MirrorCS"),sQuery(id+"F0.wireOp",EDGE,"E138.MirrorCS"),sQuery(id+"F0.wireOp",EDGE,"E139.MirrorCS"),sQuery(id+"F0.wireOp",EDGE,"E140.MirrorCS"),sQuery(id+"F0.wireOp",EDGE,"E141.MirrorCS"),sQuery(id+"F0.wireOp",EDGE,"E142.MirrorCS"),sQuery(id+"F0.wireOp",EDGE,"E143.MirrorCS"),sQuery(id+"F0.wireOp",EDGE,"E145.MirrorCS"),sQuery(id+"F0.wireOp",EDGE,"E146.MirrorCS"),sQuery(id+"F0.wireOp",EDGE,"E148.MirrorCS"),sQuery(id+"F0.wireOp",EDGE,"E150.MirrorCS"),sQuery(id+"F0.wireOp",EDGE,"E152.MirrorCS"),sQuery(id+"F0.wireOp",EDGE,"E153.MirrorCS"),sQuery(id+"F0.wireOp",EDGE,"E154.MirrorCS"),sQuery(id+"F0.wireOp",EDGE,"E155.MirrorCS"),sQuery(id+"F0.wireOp",EDGE,"E156.MirrorCS"),sQuery(id+"F0.wireOp",EDGE,"E158.MirrorCS"),sQuery(id+"F0.wireOp",EDGE,"E161.MirrorCS"),sQuery(id+"F0.wireOp",EDGE,"E162.MirrorCS")])]});
            var Q1;
            Q1=makeQuery(id+"F1.opExtrude","CAP_EDGE",EDGE,{"disambiguationData":[OSD([sQuery(id+"F0.wireOp",EDGE,"E59.MirrorCS"),sQuery(id+"F0.wireOp",EDGE,"E120.MirrorCS")])],"isStart":true});
            transform(context, id + "F3", {"entities" : qUnion([Q0]), "transformType" : TransformType.ROTATION, "transformAxis" : qUnion([Q1]), "angle" : 90 * degree, "makeCopy" : true});
        }
        {
            var Q0;
            Q0=makeQuery(id+"F3.opPattern","COPY",FACE,{"derivedFrom":makeQuery(id+"F1.opExtrude","CAP_FACE",FACE,{"disambiguationData":[OSD([sQuery(id+"F0.wireOp",EDGE,"E0"),sQuery(id+"F0.wireOp",EDGE,"E1"),sQuery(id+"F0.wireOp",EDGE,"E4.filletArc"),sQuery(id+"F0.wireOp",EDGE,"E5.bottom"),sQuery(id+"F0.wireOp",EDGE,"E5.top"),sQuery(id+"F0.wireOp",EDGE,"E5.left"),sQuery(id+"F0.wireOp",EDGE,"E5.right"),sQuery(id+"F0.wireOp",EDGE,"E6"),sQuery(id+"F0.wireOp",EDGE,"E7"),sQuery(id+"F0.wireOp",EDGE,"E8"),sQuery(id+"F0.wireOp",EDGE,"E9"),sQuery(id+"F0.wireOp",EDGE,"E10"),sQuery(id+"F0.wireOp",EDGE,"E11"),sQuery(id+"F0.wireOp",EDGE,"E12"),sQuery(id+"F0.wireOp",EDGE,"E13"),sQuery(id+"F0.wireOp",EDGE,"E15"),sQuery(id+"F0.wireOp",EDGE,"E16"),sQuery(id+"F0.wireOp",EDGE,"E17"),sQuery(id+"F0.wireOp",EDGE,"E18.filletArc"),sQuery(id+"F0.wireOp",EDGE,"E19.filletArc"),sQuery(id+"F0.wireOp",EDGE,"E20.filletArc"),sQuery(id+"F0.wireOp",EDGE,"E21.filletArc"),sQuery(id+"F0.wireOp",EDGE,"E22.filletArc"),sQuery(id+"F0.wireOp",EDGE,"E23.filletArc"),sQuery(id+"F0.wireOp",EDGE,"E24.MirrorCS"),sQuery(id+"F0.wireOp",EDGE,"E25.MirrorCS"),sQuery(id+"F0.wireOp",EDGE,"E26.MirrorCS"),sQuery(id+"F0.wireOp",EDGE,"E27.MirrorCS"),sQuery(id+"F0.wireOp",EDGE,"E28.MirrorCS"),sQuery(id+"F0.wireOp",EDGE,"E29.MirrorCS"),sQuery(id+"F0.wireOp",EDGE,"E30.MirrorCS"),sQuery(id+"F0.wireOp",EDGE,"E31.MirrorCS"),sQuery(id+"F0.wireOp",EDGE,"E32.MirrorCS"),sQuery(id+"F0.wireOp",EDGE,"E33.MirrorCS"),sQuery(id+"F0.wireOp",EDGE,"E34.MirrorCS"),sQuery(id+"F0.wireOp",EDGE,"E35.MirrorCS"),sQuery(id+"F0.wireOp",EDGE,"E36.MirrorCS"),sQuery(id+"F0.wireOp",EDGE,"E37.MirrorCS"),sQuery(id+"F0.wireOp",EDGE,"E38.MirrorCS"),sQuery(id+"F0.wireOp",EDGE,"E39.MirrorCS"),sQuery(id+"F0.wireOp",EDGE,"E40.MirrorCS"),sQuery(id+"F0.wireOp",EDGE,"E41.MirrorCS"),sQuery(id+"F0.wireOp",EDGE,"E42.MirrorCS"),sQuery(id+"F0.wireOp",EDGE,"E43.MirrorCS"),sQuery(id+"F0.wireOp",EDGE,"E44.MirrorCS"),sQuery(id+"F0.wireOp",EDGE,"E45.MirrorCS"),sQuery(id+"F0.wireOp",EDGE,"E46.MirrorCS"),sQuery(id+"F0.wireOp",EDGE,"E47.MirrorCS"),sQuery(id+"F0.wireOp",EDGE,"E48.MirrorCS"),sQuery(id+"F0.wireOp",EDGE,"E50.MirrorCS"),sQuery(id+"F0.wireOp",EDGE,"E51.MirrorCS"),sQuery(id+"F0.wireOp",EDGE,"E52.MirrorCS"),sQuery(id+"F0.wireOp",EDGE,"E53.MirrorCS"),sQuery(id+"F0.wireOp",EDGE,"E54.MirrorCS"),sQuery(id+"F0.wireOp",EDGE,"E59.MirrorCS"),sQuery(id+"F0.wireOp",EDGE,"E60.MirrorCS"),sQuery(id+"F0.wireOp",EDGE,"E61.MirrorCS"),sQuery(id+"F0.wireOp",EDGE,"E62.MirrorCS"),sQuery(id+"F0.wireOp",EDGE,"E63.MirrorCS"),sQuery(id+"F0.wireOp",EDGE,"E64.MirrorCS"),sQuery(id+"F0.wireOp",EDGE,"E65.MirrorCS"),sQuery(id+"F0.wireOp",EDGE,"E66.MirrorCS"),sQuery(id+"F0.wireOp",EDGE,"E67.MirrorCS"),sQuery(id+"F0.wireOp",EDGE,"E68.MirrorCS"),sQuery(id+"F0.wireOp",EDGE,"E69.MirrorCS"),sQuery(id+"F0.wireOp",EDGE,"E71.MirrorCS"),sQuery(id+"F0.wireOp",EDGE,"E73.MirrorCS"),sQuery(id+"F0.wireOp",EDGE,"E74.MirrorCS"),sQuery(id+"F0.wireOp",EDGE,"E75.MirrorCS"),sQuery(id+"F0.wireOp",EDGE,"E76.MirrorCS"),sQuery(id+"F0.wireOp",EDGE,"E77.MirrorCS"),sQuery(id+"F0.wireOp",EDGE,"E79.MirrorCS"),sQuery(id+"F0.wireOp",EDGE,"E80.MirrorCS"),sQuery(id+"F0.wireOp",EDGE,"E81.MirrorCS"),sQuery(id+"F0.wireOp",EDGE,"E82.MirrorCS"),sQuery(id+"F0.wireOp",EDGE,"E83.MirrorCS"),sQuery(id+"F0.wireOp",EDGE,"E84.MirrorCS"),sQuery(id+"F0.wireOp",EDGE,"E85.MirrorCS"),sQuery(id+"F0.wireOp",EDGE,"E86.MirrorCS"),sQuery(id+"F0.wireOp",EDGE,"E87.MirrorCS"),sQuery(id+"F0.wireOp",EDGE,"E88.MirrorCS"),sQuery(id+"F0.wireOp",EDGE,"E89.MirrorCS"),sQuery(id+"F0.wireOp",EDGE,"E90.MirrorCS"),sQuery(id+"F0.wireOp",EDGE,"E91.MirrorCS"),sQuery(id+"F0.wireOp",EDGE,"E92.MirrorCS"),sQuery(id+"F0.wireOp",EDGE,"E93.MirrorCS"),sQuery(id+"F0.wireOp",EDGE,"E94.MirrorCS"),sQuery(id+"F0.wireOp",EDGE,"E95.MirrorCS"),sQuery(id+"F0.wireOp",EDGE,"E96.MirrorCS"),sQuery(id+"F0.wireOp",EDGE,"E97.MirrorCS"),sQuery(id+"F0.wireOp",EDGE,"E98.MirrorCS"),sQuery(id+"F0.wireOp",EDGE,"E99.MirrorCS"),sQuery(id+"F0.wireOp",EDGE,"E100.MirrorCS"),sQuery(id+"F0.wireOp",EDGE,"E101.MirrorCS"),sQuery(id+"F0.wireOp",EDGE,"E102.MirrorCS"),sQuery(id+"F0.wireOp",EDGE,"E103.MirrorCS"),sQuery(id+"F0.wireOp",EDGE,"E104.MirrorCS"),sQuery(id+"F0.wireOp",EDGE,"E105.MirrorCS"),sQuery(id+"F0.wireOp",EDGE,"E106.MirrorCS"),sQuery(id+"F0.wireOp",EDGE,"E107.MirrorCS"),sQuery(id+"F0.wireOp",EDGE,"E108.MirrorCS"),sQuery(id+"F0.wireOp",EDGE,"E109.MirrorCS"),sQuery(id+"F0.wireOp",EDGE,"E110.MirrorCS"),sQuery(id+"F0.wireOp",EDGE,"E111.MirrorCS"),sQuery(id+"F0.wireOp",EDGE,"E112.MirrorCS"),sQuery(id+"F0.wireOp",EDGE,"E113.MirrorCS"),sQuery(id+"F0.wireOp",EDGE,"E114.MirrorCS"),sQuery(id+"F0.wireOp",EDGE,"E119.MirrorCS"),sQuery(id+"F0.wireOp",EDGE,"E120.MirrorCS"),sQuery(id+"F0.wireOp",EDGE,"E121.MirrorCS"),sQuery(id+"F0.wireOp",EDGE,"E125.MirrorCS"),sQuery(id+"F0.wireOp",EDGE,"E126.MirrorCS"),sQuery(id+"F0.wireOp",EDGE,"E127.MirrorCS"),sQuery(id+"F0.wireOp",EDGE,"E128.MirrorCS"),sQuery(id+"F0.wireOp",EDGE,"E129.MirrorCS"),sQuery(id+"F0.wireOp",EDGE,"E130.MirrorCS"),sQuery(id+"F0.wireOp",EDGE,"E131.MirrorCS"),sQuery(id+"F0.wireOp",EDGE,"E132.MirrorCS"),sQuery(id+"F0.wireOp",EDGE,"E133.MirrorCS"),sQuery(id+"F0.wireOp",EDGE,"E134.MirrorCS"),sQuery(id+"F0.wireOp",EDGE,"E135.MirrorCS"),sQuery(id+"F0.wireOp",EDGE,"E136.MirrorCS"),sQuery(id+"F0.wireOp",EDGE,"E137.MirrorCS"),sQuery(id+"F0.wireOp",EDGE,"E138.MirrorCS"),sQuery(id+"F0.wireOp",EDGE,"E139.MirrorCS"),sQuery(id+"F0.wireOp",EDGE,"E140.MirrorCS"),sQuery(id+"F0.wireOp",EDGE,"E141.MirrorCS"),sQuery(id+"F0.wireOp",EDGE,"E142.MirrorCS"),sQuery(id+"F0.wireOp",EDGE,"E143.MirrorCS"),sQuery(id+"F0.wireOp",EDGE,"E145.MirrorCS"),sQuery(id+"F0.wireOp",EDGE,"E146.MirrorCS"),sQuery(id+"F0.wireOp",EDGE,"E148.MirrorCS"),sQuery(id+"F0.wireOp",EDGE,"E150.MirrorCS"),sQuery(id+"F0.wireOp",EDGE,"E152.MirrorCS"),sQuery(id+"F0.wireOp",EDGE,"E153.MirrorCS"),sQuery(id+"F0.wireOp",EDGE,"E154.MirrorCS"),sQuery(id+"F0.wireOp",EDGE,"E155.MirrorCS"),sQuery(id+"F0.wireOp",EDGE,"E156.MirrorCS"),sQuery(id+"F0.wireOp",EDGE,"E158.MirrorCS"),sQuery(id+"F0.wireOp",EDGE,"E161.MirrorCS"),sQuery(id+"F0.wireOp",EDGE,"E162.MirrorCS")])],"isStart":false}),"instanceName":"1"});
            extrude(context, id + "F4", {"entities" : qUnion([Q0]), "operationType" : NewBodyOperationType.REMOVE, "oppositeDirection" : true, "depth" : 523 * mm});
        }
        {
            var Q0;
            Q0=makeQuery(id+"F3.opPattern","COPY",BODY,{"derivedFrom":makeQuery(id+"F1.opExtrude","SWEPT_BODY",BODY,{"disambiguationData":[OSD([sQuery(id+"F0.wireOp",EDGE,"E0"),sQuery(id+"F0.wireOp",EDGE,"E1"),sQuery(id+"F0.wireOp",EDGE,"E4.filletArc"),sQuery(id+"F0.wireOp",EDGE,"E5.bottom"),sQuery(id+"F0.wireOp",EDGE,"E5.top"),sQuery(id+"F0.wireOp",EDGE,"E5.left"),sQuery(id+"F0.wireOp",EDGE,"E5.right"),sQuery(id+"F0.wireOp",EDGE,"E6"),sQuery(id+"F0.wireOp",EDGE,"E7"),sQuery(id+"F0.wireOp",EDGE,"E8"),sQuery(id+"F0.wireOp",EDGE,"E9"),sQuery(id+"F0.wireOp",EDGE,"E10"),sQuery(id+"F0.wireOp",EDGE,"E11"),sQuery(id+"F0.wireOp",EDGE,"E12"),sQuery(id+"F0.wireOp",EDGE,"E13"),sQuery(id+"F0.wireOp",EDGE,"E15"),sQuery(id+"F0.wireOp",EDGE,"E16"),sQuery(id+"F0.wireOp",EDGE,"E17"),sQuery(id+"F0.wireOp",EDGE,"E18.filletArc"),sQuery(id+"F0.wireOp",EDGE,"E19.filletArc"),sQuery(id+"F0.wireOp",EDGE,"E20.filletArc"),sQuery(id+"F0.wireOp",EDGE,"E21.filletArc"),sQuery(id+"F0.wireOp",EDGE,"E22.filletArc"),sQuery(id+"F0.wireOp",EDGE,"E23.filletArc"),sQuery(id+"F0.wireOp",EDGE,"E24.MirrorCS"),sQuery(id+"F0.wireOp",EDGE,"E25.MirrorCS"),sQuery(id+"F0.wireOp",EDGE,"E26.MirrorCS"),sQuery(id+"F0.wireOp",EDGE,"E27.MirrorCS"),sQuery(id+"F0.wireOp",EDGE,"E28.MirrorCS"),sQuery(id+"F0.wireOp",EDGE,"E29.MirrorCS"),sQuery(id+"F0.wireOp",EDGE,"E30.MirrorCS"),sQuery(id+"F0.wireOp",EDGE,"E31.MirrorCS"),sQuery(id+"F0.wireOp",EDGE,"E32.MirrorCS"),sQuery(id+"F0.wireOp",EDGE,"E33.MirrorCS"),sQuery(id+"F0.wireOp",EDGE,"E34.MirrorCS"),sQuery(id+"F0.wireOp",EDGE,"E35.MirrorCS"),sQuery(id+"F0.wireOp",EDGE,"E36.MirrorCS"),sQuery(id+"F0.wireOp",EDGE,"E37.MirrorCS"),sQuery(id+"F0.wireOp",EDGE,"E38.MirrorCS"),sQuery(id+"F0.wireOp",EDGE,"E39.MirrorCS"),sQuery(id+"F0.wireOp",EDGE,"E40.MirrorCS"),sQuery(id+"F0.wireOp",EDGE,"E41.MirrorCS"),sQuery(id+"F0.wireOp",EDGE,"E42.MirrorCS"),sQuery(id+"F0.wireOp",EDGE,"E43.MirrorCS"),sQuery(id+"F0.wireOp",EDGE,"E44.MirrorCS"),sQuery(id+"F0.wireOp",EDGE,"E45.MirrorCS"),sQuery(id+"F0.wireOp",EDGE,"E46.MirrorCS"),sQuery(id+"F0.wireOp",EDGE,"E47.MirrorCS"),sQuery(id+"F0.wireOp",EDGE,"E48.MirrorCS"),sQuery(id+"F0.wireOp",EDGE,"E50.MirrorCS"),sQuery(id+"F0.wireOp",EDGE,"E51.MirrorCS"),sQuery(id+"F0.wireOp",EDGE,"E52.MirrorCS"),sQuery(id+"F0.wireOp",EDGE,"E53.MirrorCS"),sQuery(id+"F0.wireOp",EDGE,"E54.MirrorCS"),sQuery(id+"F0.wireOp",EDGE,"E59.MirrorCS"),sQuery(id+"F0.wireOp",EDGE,"E60.MirrorCS"),sQuery(id+"F0.wireOp",EDGE,"E61.MirrorCS"),sQuery(id+"F0.wireOp",EDGE,"E62.MirrorCS"),sQuery(id+"F0.wireOp",EDGE,"E63.MirrorCS"),sQuery(id+"F0.wireOp",EDGE,"E64.MirrorCS"),sQuery(id+"F0.wireOp",EDGE,"E65.MirrorCS"),sQuery(id+"F0.wireOp",EDGE,"E66.MirrorCS"),sQuery(id+"F0.wireOp",EDGE,"E67.MirrorCS"),sQuery(id+"F0.wireOp",EDGE,"E68.MirrorCS"),sQuery(id+"F0.wireOp",EDGE,"E69.MirrorCS"),sQuery(id+"F0.wireOp",EDGE,"E71.MirrorCS"),sQuery(id+"F0.wireOp",EDGE,"E73.MirrorCS"),sQuery(id+"F0.wireOp",EDGE,"E74.MirrorCS"),sQuery(id+"F0.wireOp",EDGE,"E75.MirrorCS"),sQuery(id+"F0.wireOp",EDGE,"E76.MirrorCS"),sQuery(id+"F0.wireOp",EDGE,"E77.MirrorCS"),sQuery(id+"F0.wireOp",EDGE,"E79.MirrorCS"),sQuery(id+"F0.wireOp",EDGE,"E80.MirrorCS"),sQuery(id+"F0.wireOp",EDGE,"E81.MirrorCS"),sQuery(id+"F0.wireOp",EDGE,"E82.MirrorCS"),sQuery(id+"F0.wireOp",EDGE,"E83.MirrorCS"),sQuery(id+"F0.wireOp",EDGE,"E84.MirrorCS"),sQuery(id+"F0.wireOp",EDGE,"E85.MirrorCS"),sQuery(id+"F0.wireOp",EDGE,"E86.MirrorCS"),sQuery(id+"F0.wireOp",EDGE,"E87.MirrorCS"),sQuery(id+"F0.wireOp",EDGE,"E88.MirrorCS"),sQuery(id+"F0.wireOp",EDGE,"E89.MirrorCS"),sQuery(id+"F0.wireOp",EDGE,"E90.MirrorCS"),sQuery(id+"F0.wireOp",EDGE,"E91.MirrorCS"),sQuery(id+"F0.wireOp",EDGE,"E92.MirrorCS"),sQuery(id+"F0.wireOp",EDGE,"E93.MirrorCS"),sQuery(id+"F0.wireOp",EDGE,"E94.MirrorCS"),sQuery(id+"F0.wireOp",EDGE,"E95.MirrorCS"),sQuery(id+"F0.wireOp",EDGE,"E96.MirrorCS"),sQuery(id+"F0.wireOp",EDGE,"E97.MirrorCS"),sQuery(id+"F0.wireOp",EDGE,"E98.MirrorCS"),sQuery(id+"F0.wireOp",EDGE,"E99.MirrorCS"),sQuery(id+"F0.wireOp",EDGE,"E100.MirrorCS"),sQuery(id+"F0.wireOp",EDGE,"E101.MirrorCS"),sQuery(id+"F0.wireOp",EDGE,"E102.MirrorCS"),sQuery(id+"F0.wireOp",EDGE,"E103.MirrorCS"),sQuery(id+"F0.wireOp",EDGE,"E104.MirrorCS"),sQuery(id+"F0.wireOp",EDGE,"E105.MirrorCS"),sQuery(id+"F0.wireOp",EDGE,"E106.MirrorCS"),sQuery(id+"F0.wireOp",EDGE,"E107.MirrorCS"),sQuery(id+"F0.wireOp",EDGE,"E108.MirrorCS"),sQuery(id+"F0.wireOp",EDGE,"E109.MirrorCS"),sQuery(id+"F0.wireOp",EDGE,"E110.MirrorCS"),sQuery(id+"F0.wireOp",EDGE,"E111.MirrorCS"),sQuery(id+"F0.wireOp",EDGE,"E112.MirrorCS"),sQuery(id+"F0.wireOp",EDGE,"E113.MirrorCS"),sQuery(id+"F0.wireOp",EDGE,"E114.MirrorCS"),sQuery(id+"F0.wireOp",EDGE,"E119.MirrorCS"),sQuery(id+"F0.wireOp",EDGE,"E120.MirrorCS"),sQuery(id+"F0.wireOp",EDGE,"E121.MirrorCS"),sQuery(id+"F0.wireOp",EDGE,"E125.MirrorCS"),sQuery(id+"F0.wireOp",EDGE,"E126.MirrorCS"),sQuery(id+"F0.wireOp",EDGE,"E127.MirrorCS"),sQuery(id+"F0.wireOp",EDGE,"E128.MirrorCS"),sQuery(id+"F0.wireOp",EDGE,"E129.MirrorCS"),sQuery(id+"F0.wireOp",EDGE,"E130.MirrorCS"),sQuery(id+"F0.wireOp",EDGE,"E131.MirrorCS"),sQuery(id+"F0.wireOp",EDGE,"E132.MirrorCS"),sQuery(id+"F0.wireOp",EDGE,"E133.MirrorCS"),sQuery(id+"F0.wireOp",EDGE,"E134.MirrorCS"),sQuery(id+"F0.wireOp",EDGE,"E135.MirrorCS"),sQuery(id+"F0.wireOp",EDGE,"E136.MirrorCS"),sQuery(id+"F0.wireOp",EDGE,"E137.MirrorCS"),sQuery(id+"F0.wireOp",EDGE,"E138.MirrorCS"),sQuery(id+"F0.wireOp",EDGE,"E139.MirrorCS"),sQuery(id+"F0.wireOp",EDGE,"E140.MirrorCS"),sQuery(id+"F0.wireOp",EDGE,"E141.MirrorCS"),sQuery(id+"F0.wireOp",EDGE,"E142.MirrorCS"),sQuery(id+"F0.wireOp",EDGE,"E143.MirrorCS"),sQuery(id+"F0.wireOp",EDGE,"E145.MirrorCS"),sQuery(id+"F0.wireOp",EDGE,"E146.MirrorCS"),sQuery(id+"F0.wireOp",EDGE,"E148.MirrorCS"),sQuery(id+"F0.wireOp",EDGE,"E150.MirrorCS"),sQuery(id+"F0.wireOp",EDGE,"E152.MirrorCS"),sQuery(id+"F0.wireOp",EDGE,"E153.MirrorCS"),sQuery(id+"F0.wireOp",EDGE,"E154.MirrorCS"),sQuery(id+"F0.wireOp",EDGE,"E155.MirrorCS"),sQuery(id+"F0.wireOp",EDGE,"E156.MirrorCS"),sQuery(id+"F0.wireOp",EDGE,"E158.MirrorCS"),sQuery(id+"F0.wireOp",EDGE,"E161.MirrorCS"),sQuery(id+"F0.wireOp",EDGE,"E162.MirrorCS")])]}),"instanceName":"1"});
            transform(context, id + "F5", {"entities" : qUnion([Q0]), "transformType" : TransformType.TRANSLATION_3D, "dx" : 0 * mm, "dy" : -655 * mm, "dz" : 0 * mm, "makeCopy" : true});
        }
        {
            var Q0;
            Q0=qCreatedBy(makeId("Right.planeOp"),FACE);
            var sketch = newSketch(context, id + "F6", { "sketchPlane" : qUnion([Q0])});
            skLineSegment(sketch, "E163", {"start": v(0, 0) * mm, "end": v(-174.17, 0) * mm});
            skSolve(sketch);
        }
        {
            var Q0;
            Q0=makeQuery(id+"F3.opPattern","COPY",BODY,{"derivedFrom":makeQuery(id+"F1.opExtrude","SWEPT_BODY",BODY,{"disambiguationData":[OSD([sQuery(id+"F0.wireOp",EDGE,"E0"),sQuery(id+"F0.wireOp",EDGE,"E1"),sQuery(id+"F0.wireOp",EDGE,"E4.filletArc"),sQuery(id+"F0.wireOp",EDGE,"E5.bottom"),sQuery(id+"F0.wireOp",EDGE,"E5.top"),sQuery(id+"F0.wireOp",EDGE,"E5.left"),sQuery(id+"F0.wireOp",EDGE,"E5.right"),sQuery(id+"F0.wireOp",EDGE,"E6"),sQuery(id+"F0.wireOp",EDGE,"E7"),sQuery(id+"F0.wireOp",EDGE,"E8"),sQuery(id+"F0.wireOp",EDGE,"E9"),sQuery(id+"F0.wireOp",EDGE,"E10"),sQuery(id+"F0.wireOp",EDGE,"E11"),sQuery(id+"F0.wireOp",EDGE,"E12"),sQuery(id+"F0.wireOp",EDGE,"E13"),sQuery(id+"F0.wireOp",EDGE,"E15"),sQuery(id+"F0.wireOp",EDGE,"E16"),sQuery(id+"F0.wireOp",EDGE,"E17"),sQuery(id+"F0.wireOp",EDGE,"E18.filletArc"),sQuery(id+"F0.wireOp",EDGE,"E19.filletArc"),sQuery(id+"F0.wireOp",EDGE,"E20.filletArc"),sQuery(id+"F0.wireOp",EDGE,"E21.filletArc"),sQuery(id+"F0.wireOp",EDGE,"E22.filletArc"),sQuery(id+"F0.wireOp",EDGE,"E23.filletArc"),sQuery(id+"F0.wireOp",EDGE,"E24.MirrorCS"),sQuery(id+"F0.wireOp",EDGE,"E25.MirrorCS"),sQuery(id+"F0.wireOp",EDGE,"E26.MirrorCS"),sQuery(id+"F0.wireOp",EDGE,"E27.MirrorCS"),sQuery(id+"F0.wireOp",EDGE,"E28.MirrorCS"),sQuery(id+"F0.wireOp",EDGE,"E29.MirrorCS"),sQuery(id+"F0.wireOp",EDGE,"E30.MirrorCS"),sQuery(id+"F0.wireOp",EDGE,"E31.MirrorCS"),sQuery(id+"F0.wireOp",EDGE,"E32.MirrorCS"),sQuery(id+"F0.wireOp",EDGE,"E33.MirrorCS"),sQuery(id+"F0.wireOp",EDGE,"E34.MirrorCS"),sQuery(id+"F0.wireOp",EDGE,"E35.MirrorCS"),sQuery(id+"F0.wireOp",EDGE,"E36.MirrorCS"),sQuery(id+"F0.wireOp",EDGE,"E37.MirrorCS"),sQuery(id+"F0.wireOp",EDGE,"E38.MirrorCS"),sQuery(id+"F0.wireOp",EDGE,"E39.MirrorCS"),sQuery(id+"F0.wireOp",EDGE,"E40.MirrorCS"),sQuery(id+"F0.wireOp",EDGE,"E41.MirrorCS"),sQuery(id+"F0.wireOp",EDGE,"E42.MirrorCS"),sQuery(id+"F0.wireOp",EDGE,"E43.MirrorCS"),sQuery(id+"F0.wireOp",EDGE,"E44.MirrorCS"),sQuery(id+"F0.wireOp",EDGE,"E45.MirrorCS"),sQuery(id+"F0.wireOp",EDGE,"E46.MirrorCS"),sQuery(id+"F0.wireOp",EDGE,"E47.MirrorCS"),sQuery(id+"F0.wireOp",EDGE,"E48.MirrorCS"),sQuery(id+"F0.wireOp",EDGE,"E50.MirrorCS"),sQuery(id+"F0.wireOp",EDGE,"E51.MirrorCS"),sQuery(id+"F0.wireOp",EDGE,"E52.MirrorCS"),sQuery(id+"F0.wireOp",EDGE,"E53.MirrorCS"),sQuery(id+"F0.wireOp",EDGE,"E54.MirrorCS"),sQuery(id+"F0.wireOp",EDGE,"E59.MirrorCS"),sQuery(id+"F0.wireOp",EDGE,"E60.MirrorCS"),sQuery(id+"F0.wireOp",EDGE,"E61.MirrorCS"),sQuery(id+"F0.wireOp",EDGE,"E62.MirrorCS"),sQuery(id+"F0.wireOp",EDGE,"E63.MirrorCS"),sQuery(id+"F0.wireOp",EDGE,"E64.MirrorCS"),sQuery(id+"F0.wireOp",EDGE,"E65.MirrorCS"),sQuery(id+"F0.wireOp",EDGE,"E66.MirrorCS"),sQuery(id+"F0.wireOp",EDGE,"E67.MirrorCS"),sQuery(id+"F0.wireOp",EDGE,"E68.MirrorCS"),sQuery(id+"F0.wireOp",EDGE,"E69.MirrorCS"),sQuery(id+"F0.wireOp",EDGE,"E71.MirrorCS"),sQuery(id+"F0.wireOp",EDGE,"E73.MirrorCS"),sQuery(id+"F0.wireOp",EDGE,"E74.MirrorCS"),sQuery(id+"F0.wireOp",EDGE,"E75.MirrorCS"),sQuery(id+"F0.wireOp",EDGE,"E76.MirrorCS"),sQuery(id+"F0.wireOp",EDGE,"E77.MirrorCS"),sQuery(id+"F0.wireOp",EDGE,"E79.MirrorCS"),sQuery(id+"F0.wireOp",EDGE,"E80.MirrorCS"),sQuery(id+"F0.wireOp",EDGE,"E81.MirrorCS"),sQuery(id+"F0.wireOp",EDGE,"E82.MirrorCS"),sQuery(id+"F0.wireOp",EDGE,"E83.MirrorCS"),sQuery(id+"F0.wireOp",EDGE,"E84.MirrorCS"),sQuery(id+"F0.wireOp",EDGE,"E85.MirrorCS"),sQuery(id+"F0.wireOp",EDGE,"E86.MirrorCS"),sQuery(id+"F0.wireOp",EDGE,"E87.MirrorCS"),sQuery(id+"F0.wireOp",EDGE,"E88.MirrorCS"),sQuery(id+"F0.wireOp",EDGE,"E89.MirrorCS"),sQuery(id+"F0.wireOp",EDGE,"E90.MirrorCS"),sQuery(id+"F0.wireOp",EDGE,"E91.MirrorCS"),sQuery(id+"F0.wireOp",EDGE,"E92.MirrorCS"),sQuery(id+"F0.wireOp",EDGE,"E93.MirrorCS"),sQuery(id+"F0.wireOp",EDGE,"E94.MirrorCS"),sQuery(id+"F0.wireOp",EDGE,"E95.MirrorCS"),sQuery(id+"F0.wireOp",EDGE,"E96.MirrorCS"),sQuery(id+"F0.wireOp",EDGE,"E97.MirrorCS"),sQuery(id+"F0.wireOp",EDGE,"E98.MirrorCS"),sQuery(id+"F0.wireOp",EDGE,"E99.MirrorCS"),sQuery(id+"F0.wireOp",EDGE,"E100.MirrorCS"),sQuery(id+"F0.wireOp",EDGE,"E101.MirrorCS"),sQuery(id+"F0.wireOp",EDGE,"E102.MirrorCS"),sQuery(id+"F0.wireOp",EDGE,"E103.MirrorCS"),sQuery(id+"F0.wireOp",EDGE,"E104.MirrorCS"),sQuery(id+"F0.wireOp",EDGE,"E105.MirrorCS"),sQuery(id+"F0.wireOp",EDGE,"E106.MirrorCS"),sQuery(id+"F0.wireOp",EDGE,"E107.MirrorCS"),sQuery(id+"F0.wireOp",EDGE,"E108.MirrorCS"),sQuery(id+"F0.wireOp",EDGE,"E109.MirrorCS"),sQuery(id+"F0.wireOp",EDGE,"E110.MirrorCS"),sQuery(id+"F0.wireOp",EDGE,"E111.MirrorCS"),sQuery(id+"F0.wireOp",EDGE,"E112.MirrorCS"),sQuery(id+"F0.wireOp",EDGE,"E113.MirrorCS"),sQuery(id+"F0.wireOp",EDGE,"E114.MirrorCS"),sQuery(id+"F0.wireOp",EDGE,"E119.MirrorCS"),sQuery(id+"F0.wireOp",EDGE,"E120.MirrorCS"),sQuery(id+"F0.wireOp",EDGE,"E121.MirrorCS"),sQuery(id+"F0.wireOp",EDGE,"E125.MirrorCS"),sQuery(id+"F0.wireOp",EDGE,"E126.MirrorCS"),sQuery(id+"F0.wireOp",EDGE,"E127.MirrorCS"),sQuery(id+"F0.wireOp",EDGE,"E128.MirrorCS"),sQuery(id+"F0.wireOp",EDGE,"E129.MirrorCS"),sQuery(id+"F0.wireOp",EDGE,"E130.MirrorCS"),sQuery(id+"F0.wireOp",EDGE,"E131.MirrorCS"),sQuery(id+"F0.wireOp",EDGE,"E132.MirrorCS"),sQuery(id+"F0.wireOp",EDGE,"E133.MirrorCS"),sQuery(id+"F0.wireOp",EDGE,"E134.MirrorCS"),sQuery(id+"F0.wireOp",EDGE,"E135.MirrorCS"),sQuery(id+"F0.wireOp",EDGE,"E136.MirrorCS"),sQuery(id+"F0.wireOp",EDGE,"E137.MirrorCS"),sQuery(id+"F0.wireOp",EDGE,"E138.MirrorCS"),sQuery(id+"F0.wireOp",EDGE,"E139.MirrorCS"),sQuery(id+"F0.wireOp",EDGE,"E140.MirrorCS"),sQuery(id+"F0.wireOp",EDGE,"E141.MirrorCS"),sQuery(id+"F0.wireOp",EDGE,"E142.MirrorCS"),sQuery(id+"F0.wireOp",EDGE,"E143.MirrorCS"),sQuery(id+"F0.wireOp",EDGE,"E145.MirrorCS"),sQuery(id+"F0.wireOp",EDGE,"E146.MirrorCS"),sQuery(id+"F0.wireOp",EDGE,"E148.MirrorCS"),sQuery(id+"F0.wireOp",EDGE,"E150.MirrorCS"),sQuery(id+"F0.wireOp",EDGE,"E152.MirrorCS"),sQuery(id+"F0.wireOp",EDGE,"E153.MirrorCS"),sQuery(id+"F0.wireOp",EDGE,"E154.MirrorCS"),sQuery(id+"F0.wireOp",EDGE,"E155.MirrorCS"),sQuery(id+"F0.wireOp",EDGE,"E156.MirrorCS"),sQuery(id+"F0.wireOp",EDGE,"E158.MirrorCS"),sQuery(id+"F0.wireOp",EDGE,"E161.MirrorCS"),sQuery(id+"F0.wireOp",EDGE,"E162.MirrorCS")])]}),"instanceName":"1"});
            var Q1;
            Q1=makeQuery(id+"F5.opPattern","COPY",BODY,{"derivedFrom":makeQuery(id+"F3.opPattern","COPY",BODY,{"derivedFrom":makeQuery(id+"F1.opExtrude","SWEPT_BODY",BODY,{"disambiguationData":[OSD([sQuery(id+"F0.wireOp",EDGE,"E0"),sQuery(id+"F0.wireOp",EDGE,"E1"),sQuery(id+"F0.wireOp",EDGE,"E4.filletArc"),sQuery(id+"F0.wireOp",EDGE,"E5.bottom"),sQuery(id+"F0.wireOp",EDGE,"E5.top"),sQuery(id+"F0.wireOp",EDGE,"E5.left"),sQuery(id+"F0.wireOp",EDGE,"E5.right"),sQuery(id+"F0.wireOp",EDGE,"E6"),sQuery(id+"F0.wireOp",EDGE,"E7"),sQuery(id+"F0.wireOp",EDGE,"E8"),sQuery(id+"F0.wireOp",EDGE,"E9"),sQuery(id+"F0.wireOp",EDGE,"E10"),sQuery(id+"F0.wireOp",EDGE,"E11"),sQuery(id+"F0.wireOp",EDGE,"E12"),sQuery(id+"F0.wireOp",EDGE,"E13"),sQuery(id+"F0.wireOp",EDGE,"E15"),sQuery(id+"F0.wireOp",EDGE,"E16"),sQuery(id+"F0.wireOp",EDGE,"E17"),sQuery(id+"F0.wireOp",EDGE,"E18.filletArc"),sQuery(id+"F0.wireOp",EDGE,"E19.filletArc"),sQuery(id+"F0.wireOp",EDGE,"E20.filletArc"),sQuery(id+"F0.wireOp",EDGE,"E21.filletArc"),sQuery(id+"F0.wireOp",EDGE,"E22.filletArc"),sQuery(id+"F0.wireOp",EDGE,"E23.filletArc"),sQuery(id+"F0.wireOp",EDGE,"E24.MirrorCS"),sQuery(id+"F0.wireOp",EDGE,"E25.MirrorCS"),sQuery(id+"F0.wireOp",EDGE,"E26.MirrorCS"),sQuery(id+"F0.wireOp",EDGE,"E27.MirrorCS"),sQuery(id+"F0.wireOp",EDGE,"E28.MirrorCS"),sQuery(id+"F0.wireOp",EDGE,"E29.MirrorCS"),sQuery(id+"F0.wireOp",EDGE,"E30.MirrorCS"),sQuery(id+"F0.wireOp",EDGE,"E31.MirrorCS"),sQuery(id+"F0.wireOp",EDGE,"E32.MirrorCS"),sQuery(id+"F0.wireOp",EDGE,"E33.MirrorCS"),sQuery(id+"F0.wireOp",EDGE,"E34.MirrorCS"),sQuery(id+"F0.wireOp",EDGE,"E35.MirrorCS"),sQuery(id+"F0.wireOp",EDGE,"E36.MirrorCS"),sQuery(id+"F0.wireOp",EDGE,"E37.MirrorCS"),sQuery(id+"F0.wireOp",EDGE,"E38.MirrorCS"),sQuery(id+"F0.wireOp",EDGE,"E39.MirrorCS"),sQuery(id+"F0.wireOp",EDGE,"E40.MirrorCS"),sQuery(id+"F0.wireOp",EDGE,"E41.MirrorCS"),sQuery(id+"F0.wireOp",EDGE,"E42.MirrorCS"),sQuery(id+"F0.wireOp",EDGE,"E43.MirrorCS"),sQuery(id+"F0.wireOp",EDGE,"E44.MirrorCS"),sQuery(id+"F0.wireOp",EDGE,"E45.MirrorCS"),sQuery(id+"F0.wireOp",EDGE,"E46.MirrorCS"),sQuery(id+"F0.wireOp",EDGE,"E47.MirrorCS"),sQuery(id+"F0.wireOp",EDGE,"E48.MirrorCS"),sQuery(id+"F0.wireOp",EDGE,"E50.MirrorCS"),sQuery(id+"F0.wireOp",EDGE,"E51.MirrorCS"),sQuery(id+"F0.wireOp",EDGE,"E52.MirrorCS"),sQuery(id+"F0.wireOp",EDGE,"E53.MirrorCS"),sQuery(id+"F0.wireOp",EDGE,"E54.MirrorCS"),sQuery(id+"F0.wireOp",EDGE,"E59.MirrorCS"),sQuery(id+"F0.wireOp",EDGE,"E60.MirrorCS"),sQuery(id+"F0.wireOp",EDGE,"E61.MirrorCS"),sQuery(id+"F0.wireOp",EDGE,"E62.MirrorCS"),sQuery(id+"F0.wireOp",EDGE,"E63.MirrorCS"),sQuery(id+"F0.wireOp",EDGE,"E64.MirrorCS"),sQuery(id+"F0.wireOp",EDGE,"E65.MirrorCS"),sQuery(id+"F0.wireOp",EDGE,"E66.MirrorCS"),sQuery(id+"F0.wireOp",EDGE,"E67.MirrorCS"),sQuery(id+"F0.wireOp",EDGE,"E68.MirrorCS"),sQuery(id+"F0.wireOp",EDGE,"E69.MirrorCS"),sQuery(id+"F0.wireOp",EDGE,"E71.MirrorCS"),sQuery(id+"F0.wireOp",EDGE,"E73.MirrorCS"),sQuery(id+"F0.wireOp",EDGE,"E74.MirrorCS"),sQuery(id+"F0.wireOp",EDGE,"E75.MirrorCS"),sQuery(id+"F0.wireOp",EDGE,"E76.MirrorCS"),sQuery(id+"F0.wireOp",EDGE,"E77.MirrorCS"),sQuery(id+"F0.wireOp",EDGE,"E79.MirrorCS"),sQuery(id+"F0.wireOp",EDGE,"E80.MirrorCS"),sQuery(id+"F0.wireOp",EDGE,"E81.MirrorCS"),sQuery(id+"F0.wireOp",EDGE,"E82.MirrorCS"),sQuery(id+"F0.wireOp",EDGE,"E83.MirrorCS"),sQuery(id+"F0.wireOp",EDGE,"E84.MirrorCS"),sQuery(id+"F0.wireOp",EDGE,"E85.MirrorCS"),sQuery(id+"F0.wireOp",EDGE,"E86.MirrorCS"),sQuery(id+"F0.wireOp",EDGE,"E87.MirrorCS"),sQuery(id+"F0.wireOp",EDGE,"E88.MirrorCS"),sQuery(id+"F0.wireOp",EDGE,"E89.MirrorCS"),sQuery(id+"F0.wireOp",EDGE,"E90.MirrorCS"),sQuery(id+"F0.wireOp",EDGE,"E91.MirrorCS"),sQuery(id+"F0.wireOp",EDGE,"E92.MirrorCS"),sQuery(id+"F0.wireOp",EDGE,"E93.MirrorCS"),sQuery(id+"F0.wireOp",EDGE,"E94.MirrorCS"),sQuery(id+"F0.wireOp",EDGE,"E95.MirrorCS"),sQuery(id+"F0.wireOp",EDGE,"E96.MirrorCS"),sQuery(id+"F0.wireOp",EDGE,"E97.MirrorCS"),sQuery(id+"F0.wireOp",EDGE,"E98.MirrorCS"),sQuery(id+"F0.wireOp",EDGE,"E99.MirrorCS"),sQuery(id+"F0.wireOp",EDGE,"E100.MirrorCS"),sQuery(id+"F0.wireOp",EDGE,"E101.MirrorCS"),sQuery(id+"F0.wireOp",EDGE,"E102.MirrorCS"),sQuery(id+"F0.wireOp",EDGE,"E103.MirrorCS"),sQuery(id+"F0.wireOp",EDGE,"E104.MirrorCS"),sQuery(id+"F0.wireOp",EDGE,"E105.MirrorCS"),sQuery(id+"F0.wireOp",EDGE,"E106.MirrorCS"),sQuery(id+"F0.wireOp",EDGE,"E107.MirrorCS"),sQuery(id+"F0.wireOp",EDGE,"E108.MirrorCS"),sQuery(id+"F0.wireOp",EDGE,"E109.MirrorCS"),sQuery(id+"F0.wireOp",EDGE,"E110.MirrorCS"),sQuery(id+"F0.wireOp",EDGE,"E111.MirrorCS"),sQuery(id+"F0.wireOp",EDGE,"E112.MirrorCS"),sQuery(id+"F0.wireOp",EDGE,"E113.MirrorCS"),sQuery(id+"F0.wireOp",EDGE,"E114.MirrorCS"),sQuery(id+"F0.wireOp",EDGE,"E119.MirrorCS"),sQuery(id+"F0.wireOp",EDGE,"E120.MirrorCS"),sQuery(id+"F0.wireOp",EDGE,"E121.MirrorCS"),sQuery(id+"F0.wireOp",EDGE,"E125.MirrorCS"),sQuery(id+"F0.wireOp",EDGE,"E126.MirrorCS"),sQuery(id+"F0.wireOp",EDGE,"E127.MirrorCS"),sQuery(id+"F0.wireOp",EDGE,"E128.MirrorCS"),sQuery(id+"F0.wireOp",EDGE,"E129.MirrorCS"),sQuery(id+"F0.wireOp",EDGE,"E130.MirrorCS"),sQuery(id+"F0.wireOp",EDGE,"E131.MirrorCS"),sQuery(id+"F0.wireOp",EDGE,"E132.MirrorCS"),sQuery(id+"F0.wireOp",EDGE,"E133.MirrorCS"),sQuery(id+"F0.wireOp",EDGE,"E134.MirrorCS"),sQuery(id+"F0.wireOp",EDGE,"E135.MirrorCS"),sQuery(id+"F0.wireOp",EDGE,"E136.MirrorCS"),sQuery(id+"F0.wireOp",EDGE,"E137.MirrorCS"),sQuery(id+"F0.wireOp",EDGE,"E138.MirrorCS"),sQuery(id+"F0.wireOp",EDGE,"E139.MirrorCS"),sQuery(id+"F0.wireOp",EDGE,"E140.MirrorCS"),sQuery(id+"F0.wireOp",EDGE,"E141.MirrorCS"),sQuery(id+"F0.wireOp",EDGE,"E142.MirrorCS"),sQuery(id+"F0.wireOp",EDGE,"E143.MirrorCS"),sQuery(id+"F0.wireOp",EDGE,"E145.MirrorCS"),sQuery(id+"F0.wireOp",EDGE,"E146.MirrorCS"),sQuery(id+"F0.wireOp",EDGE,"E148.MirrorCS"),sQuery(id+"F0.wireOp",EDGE,"E150.MirrorCS"),sQuery(id+"F0.wireOp",EDGE,"E152.MirrorCS"),sQuery(id+"F0.wireOp",EDGE,"E153.MirrorCS"),sQuery(id+"F0.wireOp",EDGE,"E154.MirrorCS"),sQuery(id+"F0.wireOp",EDGE,"E155.MirrorCS"),sQuery(id+"F0.wireOp",EDGE,"E156.MirrorCS"),sQuery(id+"F0.wireOp",EDGE,"E158.MirrorCS"),sQuery(id+"F0.wireOp",EDGE,"E161.MirrorCS"),sQuery(id+"F0.wireOp",EDGE,"E162.MirrorCS")])]}),"instanceName":"1"}),"instanceName":"1"});
            var Q2;
            Q2=makeQuery(id+"F1.opExtrude","SWEPT_BODY",BODY,{"disambiguationData":[OSD([sQuery(id+"F0.wireOp",EDGE,"E0"),sQuery(id+"F0.wireOp",EDGE,"E1"),sQuery(id+"F0.wireOp",EDGE,"E4.filletArc"),sQuery(id+"F0.wireOp",EDGE,"E5.bottom"),sQuery(id+"F0.wireOp",EDGE,"E5.top"),sQuery(id+"F0.wireOp",EDGE,"E5.left"),sQuery(id+"F0.wireOp",EDGE,"E5.right"),sQuery(id+"F0.wireOp",EDGE,"E6"),sQuery(id+"F0.wireOp",EDGE,"E7"),sQuery(id+"F0.wireOp",EDGE,"E8"),sQuery(id+"F0.wireOp",EDGE,"E9"),sQuery(id+"F0.wireOp",EDGE,"E10"),sQuery(id+"F0.wireOp",EDGE,"E11"),sQuery(id+"F0.wireOp",EDGE,"E12"),sQuery(id+"F0.wireOp",EDGE,"E13"),sQuery(id+"F0.wireOp",EDGE,"E15"),sQuery(id+"F0.wireOp",EDGE,"E16"),sQuery(id+"F0.wireOp",EDGE,"E17"),sQuery(id+"F0.wireOp",EDGE,"E18.filletArc"),sQuery(id+"F0.wireOp",EDGE,"E19.filletArc"),sQuery(id+"F0.wireOp",EDGE,"E20.filletArc"),sQuery(id+"F0.wireOp",EDGE,"E21.filletArc"),sQuery(id+"F0.wireOp",EDGE,"E22.filletArc"),sQuery(id+"F0.wireOp",EDGE,"E23.filletArc"),sQuery(id+"F0.wireOp",EDGE,"E24.MirrorCS"),sQuery(id+"F0.wireOp",EDGE,"E25.MirrorCS"),sQuery(id+"F0.wireOp",EDGE,"E26.MirrorCS"),sQuery(id+"F0.wireOp",EDGE,"E27.MirrorCS"),sQuery(id+"F0.wireOp",EDGE,"E28.MirrorCS"),sQuery(id+"F0.wireOp",EDGE,"E29.MirrorCS"),sQuery(id+"F0.wireOp",EDGE,"E30.MirrorCS"),sQuery(id+"F0.wireOp",EDGE,"E31.MirrorCS"),sQuery(id+"F0.wireOp",EDGE,"E32.MirrorCS"),sQuery(id+"F0.wireOp",EDGE,"E33.MirrorCS"),sQuery(id+"F0.wireOp",EDGE,"E34.MirrorCS"),sQuery(id+"F0.wireOp",EDGE,"E35.MirrorCS"),sQuery(id+"F0.wireOp",EDGE,"E36.MirrorCS"),sQuery(id+"F0.wireOp",EDGE,"E37.MirrorCS"),sQuery(id+"F0.wireOp",EDGE,"E38.MirrorCS"),sQuery(id+"F0.wireOp",EDGE,"E39.MirrorCS"),sQuery(id+"F0.wireOp",EDGE,"E40.MirrorCS"),sQuery(id+"F0.wireOp",EDGE,"E41.MirrorCS"),sQuery(id+"F0.wireOp",EDGE,"E42.MirrorCS"),sQuery(id+"F0.wireOp",EDGE,"E43.MirrorCS"),sQuery(id+"F0.wireOp",EDGE,"E44.MirrorCS"),sQuery(id+"F0.wireOp",EDGE,"E45.MirrorCS"),sQuery(id+"F0.wireOp",EDGE,"E46.MirrorCS"),sQuery(id+"F0.wireOp",EDGE,"E47.MirrorCS"),sQuery(id+"F0.wireOp",EDGE,"E48.MirrorCS"),sQuery(id+"F0.wireOp",EDGE,"E50.MirrorCS"),sQuery(id+"F0.wireOp",EDGE,"E51.MirrorCS"),sQuery(id+"F0.wireOp",EDGE,"E52.MirrorCS"),sQuery(id+"F0.wireOp",EDGE,"E53.MirrorCS"),sQuery(id+"F0.wireOp",EDGE,"E54.MirrorCS"),sQuery(id+"F0.wireOp",EDGE,"E59.MirrorCS"),sQuery(id+"F0.wireOp",EDGE,"E60.MirrorCS"),sQuery(id+"F0.wireOp",EDGE,"E61.MirrorCS"),sQuery(id+"F0.wireOp",EDGE,"E62.MirrorCS"),sQuery(id+"F0.wireOp",EDGE,"E63.MirrorCS"),sQuery(id+"F0.wireOp",EDGE,"E64.MirrorCS"),sQuery(id+"F0.wireOp",EDGE,"E65.MirrorCS"),sQuery(id+"F0.wireOp",EDGE,"E66.MirrorCS"),sQuery(id+"F0.wireOp",EDGE,"E67.MirrorCS"),sQuery(id+"F0.wireOp",EDGE,"E68.MirrorCS"),sQuery(id+"F0.wireOp",EDGE,"E69.MirrorCS"),sQuery(id+"F0.wireOp",EDGE,"E71.MirrorCS"),sQuery(id+"F0.wireOp",EDGE,"E73.MirrorCS"),sQuery(id+"F0.wireOp",EDGE,"E74.MirrorCS"),sQuery(id+"F0.wireOp",EDGE,"E75.MirrorCS"),sQuery(id+"F0.wireOp",EDGE,"E76.MirrorCS"),sQuery(id+"F0.wireOp",EDGE,"E77.MirrorCS"),sQuery(id+"F0.wireOp",EDGE,"E79.MirrorCS"),sQuery(id+"F0.wireOp",EDGE,"E80.MirrorCS"),sQuery(id+"F0.wireOp",EDGE,"E81.MirrorCS"),sQuery(id+"F0.wireOp",EDGE,"E82.MirrorCS"),sQuery(id+"F0.wireOp",EDGE,"E83.MirrorCS"),sQuery(id+"F0.wireOp",EDGE,"E84.MirrorCS"),sQuery(id+"F0.wireOp",EDGE,"E85.MirrorCS"),sQuery(id+"F0.wireOp",EDGE,"E86.MirrorCS"),sQuery(id+"F0.wireOp",EDGE,"E87.MirrorCS"),sQuery(id+"F0.wireOp",EDGE,"E88.MirrorCS"),sQuery(id+"F0.wireOp",EDGE,"E89.MirrorCS"),sQuery(id+"F0.wireOp",EDGE,"E90.MirrorCS"),sQuery(id+"F0.wireOp",EDGE,"E91.MirrorCS"),sQuery(id+"F0.wireOp",EDGE,"E92.MirrorCS"),sQuery(id+"F0.wireOp",EDGE,"E93.MirrorCS"),sQuery(id+"F0.wireOp",EDGE,"E94.MirrorCS"),sQuery(id+"F0.wireOp",EDGE,"E95.MirrorCS"),sQuery(id+"F0.wireOp",EDGE,"E96.MirrorCS"),sQuery(id+"F0.wireOp",EDGE,"E97.MirrorCS"),sQuery(id+"F0.wireOp",EDGE,"E98.MirrorCS"),sQuery(id+"F0.wireOp",EDGE,"E99.MirrorCS"),sQuery(id+"F0.wireOp",EDGE,"E100.MirrorCS"),sQuery(id+"F0.wireOp",EDGE,"E101.MirrorCS"),sQuery(id+"F0.wireOp",EDGE,"E102.MirrorCS"),sQuery(id+"F0.wireOp",EDGE,"E103.MirrorCS"),sQuery(id+"F0.wireOp",EDGE,"E104.MirrorCS"),sQuery(id+"F0.wireOp",EDGE,"E105.MirrorCS"),sQuery(id+"F0.wireOp",EDGE,"E106.MirrorCS"),sQuery(id+"F0.wireOp",EDGE,"E107.MirrorCS"),sQuery(id+"F0.wireOp",EDGE,"E108.MirrorCS"),sQuery(id+"F0.wireOp",EDGE,"E109.MirrorCS"),sQuery(id+"F0.wireOp",EDGE,"E110.MirrorCS"),sQuery(id+"F0.wireOp",EDGE,"E111.MirrorCS"),sQuery(id+"F0.wireOp",EDGE,"E112.MirrorCS"),sQuery(id+"F0.wireOp",EDGE,"E113.MirrorCS"),sQuery(id+"F0.wireOp",EDGE,"E114.MirrorCS"),sQuery(id+"F0.wireOp",EDGE,"E119.MirrorCS"),sQuery(id+"F0.wireOp",EDGE,"E120.MirrorCS"),sQuery(id+"F0.wireOp",EDGE,"E121.MirrorCS"),sQuery(id+"F0.wireOp",EDGE,"E125.MirrorCS"),sQuery(id+"F0.wireOp",EDGE,"E126.MirrorCS"),sQuery(id+"F0.wireOp",EDGE,"E127.MirrorCS"),sQuery(id+"F0.wireOp",EDGE,"E128.MirrorCS"),sQuery(id+"F0.wireOp",EDGE,"E129.MirrorCS"),sQuery(id+"F0.wireOp",EDGE,"E130.MirrorCS"),sQuery(id+"F0.wireOp",EDGE,"E131.MirrorCS"),sQuery(id+"F0.wireOp",EDGE,"E132.MirrorCS"),sQuery(id+"F0.wireOp",EDGE,"E133.MirrorCS"),sQuery(id+"F0.wireOp",EDGE,"E134.MirrorCS"),sQuery(id+"F0.wireOp",EDGE,"E135.MirrorCS"),sQuery(id+"F0.wireOp",EDGE,"E136.MirrorCS"),sQuery(id+"F0.wireOp",EDGE,"E137.MirrorCS"),sQuery(id+"F0.wireOp",EDGE,"E138.MirrorCS"),sQuery(id+"F0.wireOp",EDGE,"E139.MirrorCS"),sQuery(id+"F0.wireOp",EDGE,"E140.MirrorCS"),sQuery(id+"F0.wireOp",EDGE,"E141.MirrorCS"),sQuery(id+"F0.wireOp",EDGE,"E142.MirrorCS"),sQuery(id+"F0.wireOp",EDGE,"E143.MirrorCS"),sQuery(id+"F0.wireOp",EDGE,"E145.MirrorCS"),sQuery(id+"F0.wireOp",EDGE,"E146.MirrorCS"),sQuery(id+"F0.wireOp",EDGE,"E148.MirrorCS"),sQuery(id+"F0.wireOp",EDGE,"E150.MirrorCS"),sQuery(id+"F0.wireOp",EDGE,"E152.MirrorCS"),sQuery(id+"F0.wireOp",EDGE,"E153.MirrorCS"),sQuery(id+"F0.wireOp",EDGE,"E154.MirrorCS"),sQuery(id+"F0.wireOp",EDGE,"E155.MirrorCS"),sQuery(id+"F0.wireOp",EDGE,"E156.MirrorCS"),sQuery(id+"F0.wireOp",EDGE,"E158.MirrorCS"),sQuery(id+"F0.wireOp",EDGE,"E161.MirrorCS"),sQuery(id+"F0.wireOp",EDGE,"E162.MirrorCS")])]});
            var Q3;
            Q3=sQuery(id+"F6.wireOp",EDGE,"E163");
            circularPattern(context, id + "F7", {"entities" : qUnion([Q0, Q1, Q2]), "axis" : qUnion([Q3]), "angle" : 360 * degree, "instanceCount" : 3, "equalSpace" : true});
        }
        {
            var Q0;
            Q0=makeQuery(id+"F5.opPattern","COPY",FACE,{"derivedFrom":makeQuery(id+"F3.opPattern","COPY",FACE,{"derivedFrom":makeQuery(id+"F1.opExtrude","SWEPT_FACE",FACE,{"disambiguationData":[OSD([sQuery(id+"F0.wireOp",EDGE,"E1"),sQuery(id+"F0.wireOp",EDGE,"E135.MirrorCS")])]}),"instanceName":"1"}),"instanceName":"1"});
            var sketch = newSketch(context, id + "F8", { "sketchPlane" : qUnion([Q0])});
            skLineSegment(sketch, "E164", {"start": v(0, 0) * mm, "end": v(-19.52, 11.2) * mm});
            skLineSegment(sketch, "E165", {"start": v(-19.52, 11.2) * mm, "end": v(68.54, 164.64) * mm});
            skLineSegment(sketch, "E166.1.0", {"start": v(0, 0) * mm, "end": v(0.06, -22.5) * mm});
            skLineSegment(sketch, "E166.1.1", {"start": v(0.06, -22.5) * mm, "end": v(-176.85, -22.97) * mm});
            skLineSegment(sketch, "E166.2.0", {"start": v(0, 0) * mm, "end": v(19.46, 11.3) * mm});
            skLineSegment(sketch, "E166.2.1", {"start": v(19.46, 11.3) * mm, "end": v(108.32, -141.68) * mm});
            skPoint(sketch, "E166.center", {"position": v(0, 0) * mm});
            skLineSegment(sketch, "E167", {"start": v(0, 0) * mm, "end": v(0, 45.2) * mm});
            skLineSegment(sketch, "E168", {"start": v(0, 0) * mm, "end": v(39.1, -22.5) * mm});
            skLineSegment(sketch, "E169", {"start": v(0, 0) * mm, "end": v(-39.14, -22.6) * mm});
            skSolve(sketch);
        }
        {
            var Q0;
            {var subQ0=sQuery(id+"F8.wireOp",EDGE,"E164");Q0=makeQuery(id+"F8.imprint","IMPRINT",FACE,{"disambiguationData":[TD([[makeQuery(id+"F8.imprint","IMPRINT",EDGE,{"derivedFrom":subQ0}),-1.0]])]});}
            var Q1;
            {var subQ0=sQuery(id+"F8.wireOp",EDGE,"E167");var subQ1=sQuery(id+"F8.wireOp",EDGE,"E165");var subQ2=makeQuery(id+"F8.imprint","INTERSECT",VERTEX,{"derivedFrom":[subQ1,subQ0]});Q1=makeQuery(id+"F8.imprint","IMPRINT",FACE,{"disambiguationData":[TD([[makeQuery(id+"F8.imprint","IMPRINT",EDGE,{"disambiguationData":[TD([[subQ2,1.0]])],"derivedFrom":subQ1}),-1.0]])]});}
            extrude(context, id + "F9", {"entities" : qUnion([Q0, Q1]), "operationType" : NewBodyOperationType.REMOVE, "oppositeDirection" : true, "depth" : 826 * mm});
        }
        {
            var Q0;
            {var subQ0=sQuery(id+"F8.wireOp",EDGE,"E166.2.0");Q0=makeQuery(id+"F8.imprint","IMPRINT",FACE,{"disambiguationData":[TD([[makeQuery(id+"F8.imprint","IMPRINT",EDGE,{"derivedFrom":subQ0}),-1.0]])]});}
            extrude(context, id + "F10", {"entities" : qUnion([Q0]), "operationType" : NewBodyOperationType.REMOVE, "oppositeDirection" : true, "depth" : 789 * mm});
        }
        {
            var Q0;
            {var subQ6=sQuery(id+"F8.wireOp",EDGE,"E166.1.0");Q0=makeQuery(id+"F8.imprint","IMPRINT",FACE,{"disambiguationData":[TD([[makeQuery(id+"F8.imprint","IMPRINT",EDGE,{"derivedFrom":subQ6}),-1.0]])]});}
            var Q1;
            {var subQ0=sQuery(id+"F8.wireOp",EDGE,"E169");var subQ1=sQuery(id+"F0.wireOp",EDGE,"E135.MirrorCS");var subQ4=makeQuery(id+"F5.opPattern","COPY",EDGE,{"derivedFrom":makeQuery(id+"F3.opPattern","COPY",EDGE,{"derivedFrom":makeQuery(id+"F1.opExtrude","SWEPT_EDGE",EDGE,{"disambiguationData":[OSD([sQuery(id+"F0.wireOp",EDGE,"E134.MirrorCS"),subQ1])]}),"instanceName":"1"}),"instanceName":"1"});var subQ5=makeQuery(id+"F8.imprint","INTERSECT",VERTEX,{"derivedFrom":[subQ4,subQ0]});Q1=makeQuery(id+"F8.imprint","IMPRINT",FACE,{"disambiguationData":[TD([[makeQuery(id+"F8.imprint","IMPRINT",EDGE,{"disambiguationData":[TD([[subQ5,1.0]])],"derivedFrom":subQ4}),-1.0]])]});}
            extrude(context, id + "F11", {"entities" : qUnion([Q0, Q1]), "operationType" : NewBodyOperationType.REMOVE, "oppositeDirection" : true, "depth" : 819 * mm});
        }
        {
            var Q0;
            Q0=makeQuery(id+"F10.boolean.opBoolean","SPLIT",BODY,{"disambiguationData":[OD(0.0)],"derivedFrom":makeQuery(id+"F7.opPattern","COPY",BODY,{"derivedFrom":makeQuery(id+"F5.opPattern","COPY",BODY,{"derivedFrom":makeQuery(id+"F3.opPattern","COPY",BODY,{"derivedFrom":makeQuery(id+"F1.opExtrude","SWEPT_BODY",BODY,{"disambiguationData":[OSD([sQuery(id+"F0.wireOp",EDGE,"E0"),sQuery(id+"F0.wireOp",EDGE,"E1"),sQuery(id+"F0.wireOp",EDGE,"E4.filletArc"),sQuery(id+"F0.wireOp",EDGE,"E5.bottom"),sQuery(id+"F0.wireOp",EDGE,"E5.top"),sQuery(id+"F0.wireOp",EDGE,"E5.left"),sQuery(id+"F0.wireOp",EDGE,"E5.right"),sQuery(id+"F0.wireOp",EDGE,"E6"),sQuery(id+"F0.wireOp",EDGE,"E7"),sQuery(id+"F0.wireOp",EDGE,"E8"),sQuery(id+"F0.wireOp",EDGE,"E9"),sQuery(id+"F0.wireOp",EDGE,"E10"),sQuery(id+"F0.wireOp",EDGE,"E11"),sQuery(id+"F0.wireOp",EDGE,"E12"),sQuery(id+"F0.wireOp",EDGE,"E13"),sQuery(id+"F0.wireOp",EDGE,"E15"),sQuery(id+"F0.wireOp",EDGE,"E16"),sQuery(id+"F0.wireOp",EDGE,"E17"),sQuery(id+"F0.wireOp",EDGE,"E18.filletArc"),sQuery(id+"F0.wireOp",EDGE,"E19.filletArc"),sQuery(id+"F0.wireOp",EDGE,"E20.filletArc"),sQuery(id+"F0.wireOp",EDGE,"E21.filletArc"),sQuery(id+"F0.wireOp",EDGE,"E22.filletArc"),sQuery(id+"F0.wireOp",EDGE,"E23.filletArc"),sQuery(id+"F0.wireOp",EDGE,"E24.MirrorCS"),sQuery(id+"F0.wireOp",EDGE,"E25.MirrorCS"),sQuery(id+"F0.wireOp",EDGE,"E26.MirrorCS"),sQuery(id+"F0.wireOp",EDGE,"E27.MirrorCS"),sQuery(id+"F0.wireOp",EDGE,"E28.MirrorCS"),sQuery(id+"F0.wireOp",EDGE,"E29.MirrorCS"),sQuery(id+"F0.wireOp",EDGE,"E30.MirrorCS"),sQuery(id+"F0.wireOp",EDGE,"E31.MirrorCS"),sQuery(id+"F0.wireOp",EDGE,"E32.MirrorCS"),sQuery(id+"F0.wireOp",EDGE,"E33.MirrorCS"),sQuery(id+"F0.wireOp",EDGE,"E34.MirrorCS"),sQuery(id+"F0.wireOp",EDGE,"E35.MirrorCS"),sQuery(id+"F0.wireOp",EDGE,"E36.MirrorCS"),sQuery(id+"F0.wireOp",EDGE,"E37.MirrorCS"),sQuery(id+"F0.wireOp",EDGE,"E38.MirrorCS"),sQuery(id+"F0.wireOp",EDGE,"E39.MirrorCS"),sQuery(id+"F0.wireOp",EDGE,"E40.MirrorCS"),sQuery(id+"F0.wireOp",EDGE,"E41.MirrorCS"),sQuery(id+"F0.wireOp",EDGE,"E42.MirrorCS"),sQuery(id+"F0.wireOp",EDGE,"E43.MirrorCS"),sQuery(id+"F0.wireOp",EDGE,"E44.MirrorCS"),sQuery(id+"F0.wireOp",EDGE,"E45.MirrorCS"),sQuery(id+"F0.wireOp",EDGE,"E46.MirrorCS"),sQuery(id+"F0.wireOp",EDGE,"E47.MirrorCS"),sQuery(id+"F0.wireOp",EDGE,"E48.MirrorCS"),sQuery(id+"F0.wireOp",EDGE,"E50.MirrorCS"),sQuery(id+"F0.wireOp",EDGE,"E51.MirrorCS"),sQuery(id+"F0.wireOp",EDGE,"E52.MirrorCS"),sQuery(id+"F0.wireOp",EDGE,"E53.MirrorCS"),sQuery(id+"F0.wireOp",EDGE,"E54.MirrorCS"),sQuery(id+"F0.wireOp",EDGE,"E59.MirrorCS"),sQuery(id+"F0.wireOp",EDGE,"E60.MirrorCS"),sQuery(id+"F0.wireOp",EDGE,"E61.MirrorCS"),sQuery(id+"F0.wireOp",EDGE,"E62.MirrorCS"),sQuery(id+"F0.wireOp",EDGE,"E63.MirrorCS"),sQuery(id+"F0.wireOp",EDGE,"E64.MirrorCS"),sQuery(id+"F0.wireOp",EDGE,"E65.MirrorCS"),sQuery(id+"F0.wireOp",EDGE,"E66.MirrorCS"),sQuery(id+"F0.wireOp",EDGE,"E67.MirrorCS"),sQuery(id+"F0.wireOp",EDGE,"E68.MirrorCS"),sQuery(id+"F0.wireOp",EDGE,"E69.MirrorCS"),sQuery(id+"F0.wireOp",EDGE,"E71.MirrorCS"),sQuery(id+"F0.wireOp",EDGE,"E73.MirrorCS"),sQuery(id+"F0.wireOp",EDGE,"E74.MirrorCS"),sQuery(id+"F0.wireOp",EDGE,"E75.MirrorCS"),sQuery(id+"F0.wireOp",EDGE,"E76.MirrorCS"),sQuery(id+"F0.wireOp",EDGE,"E77.MirrorCS"),sQuery(id+"F0.wireOp",EDGE,"E79.MirrorCS"),sQuery(id+"F0.wireOp",EDGE,"E80.MirrorCS"),sQuery(id+"F0.wireOp",EDGE,"E81.MirrorCS"),sQuery(id+"F0.wireOp",EDGE,"E82.MirrorCS"),sQuery(id+"F0.wireOp",EDGE,"E83.MirrorCS"),sQuery(id+"F0.wireOp",EDGE,"E84.MirrorCS"),sQuery(id+"F0.wireOp",EDGE,"E85.MirrorCS"),sQuery(id+"F0.wireOp",EDGE,"E86.MirrorCS"),sQuery(id+"F0.wireOp",EDGE,"E87.MirrorCS"),sQuery(id+"F0.wireOp",EDGE,"E88.MirrorCS"),sQuery(id+"F0.wireOp",EDGE,"E89.MirrorCS"),sQuery(id+"F0.wireOp",EDGE,"E90.MirrorCS"),sQuery(id+"F0.wireOp",EDGE,"E91.MirrorCS"),sQuery(id+"F0.wireOp",EDGE,"E92.MirrorCS"),sQuery(id+"F0.wireOp",EDGE,"E93.MirrorCS"),sQuery(id+"F0.wireOp",EDGE,"E94.MirrorCS"),sQuery(id+"F0.wireOp",EDGE,"E95.MirrorCS"),sQuery(id+"F0.wireOp",EDGE,"E96.MirrorCS"),sQuery(id+"F0.wireOp",EDGE,"E97.MirrorCS"),sQuery(id+"F0.wireOp",EDGE,"E98.MirrorCS"),sQuery(id+"F0.wireOp",EDGE,"E99.MirrorCS"),sQuery(id+"F0.wireOp",EDGE,"E100.MirrorCS"),sQuery(id+"F0.wireOp",EDGE,"E101.MirrorCS"),sQuery(id+"F0.wireOp",EDGE,"E102.MirrorCS"),sQuery(id+"F0.wireOp",EDGE,"E103.MirrorCS"),sQuery(id+"F0.wireOp",EDGE,"E104.MirrorCS"),sQuery(id+"F0.wireOp",EDGE,"E105.MirrorCS"),sQuery(id+"F0.wireOp",EDGE,"E106.MirrorCS"),sQuery(id+"F0.wireOp",EDGE,"E107.MirrorCS"),sQuery(id+"F0.wireOp",EDGE,"E108.MirrorCS"),sQuery(id+"F0.wireOp",EDGE,"E109.MirrorCS"),sQuery(id+"F0.wireOp",EDGE,"E110.MirrorCS"),sQuery(id+"F0.wireOp",EDGE,"E111.MirrorCS"),sQuery(id+"F0.wireOp",EDGE,"E112.MirrorCS"),sQuery(id+"F0.wireOp",EDGE,"E113.MirrorCS"),sQuery(id+"F0.wireOp",EDGE,"E114.MirrorCS"),sQuery(id+"F0.wireOp",EDGE,"E119.MirrorCS"),sQuery(id+"F0.wireOp",EDGE,"E120.MirrorCS"),sQuery(id+"F0.wireOp",EDGE,"E121.MirrorCS"),sQuery(id+"F0.wireOp",EDGE,"E125.MirrorCS"),sQuery(id+"F0.wireOp",EDGE,"E126.MirrorCS"),sQuery(id+"F0.wireOp",EDGE,"E127.MirrorCS"),sQuery(id+"F0.wireOp",EDGE,"E128.MirrorCS"),sQuery(id+"F0.wireOp",EDGE,"E129.MirrorCS"),sQuery(id+"F0.wireOp",EDGE,"E130.MirrorCS"),sQuery(id+"F0.wireOp",EDGE,"E131.MirrorCS"),sQuery(id+"F0.wireOp",EDGE,"E132.MirrorCS"),sQuery(id+"F0.wireOp",EDGE,"E133.MirrorCS"),sQuery(id+"F0.wireOp",EDGE,"E134.MirrorCS"),sQuery(id+"F0.wireOp",EDGE,"E135.MirrorCS"),sQuery(id+"F0.wireOp",EDGE,"E136.MirrorCS"),sQuery(id+"F0.wireOp",EDGE,"E137.MirrorCS"),sQuery(id+"F0.wireOp",EDGE,"E138.MirrorCS"),sQuery(id+"F0.wireOp",EDGE,"E139.MirrorCS"),sQuery(id+"F0.wireOp",EDGE,"E140.MirrorCS"),sQuery(id+"F0.wireOp",EDGE,"E141.MirrorCS"),sQuery(id+"F0.wireOp",EDGE,"E142.MirrorCS"),sQuery(id+"F0.wireOp",EDGE,"E143.MirrorCS"),sQuery(id+"F0.wireOp",EDGE,"E145.MirrorCS"),sQuery(id+"F0.wireOp",EDGE,"E146.MirrorCS"),sQuery(id+"F0.wireOp",EDGE,"E148.MirrorCS"),sQuery(id+"F0.wireOp",EDGE,"E150.MirrorCS"),sQuery(id+"F0.wireOp",EDGE,"E152.MirrorCS"),sQuery(id+"F0.wireOp",EDGE,"E153.MirrorCS"),sQuery(id+"F0.wireOp",EDGE,"E154.MirrorCS"),sQuery(id+"F0.wireOp",EDGE,"E155.MirrorCS"),sQuery(id+"F0.wireOp",EDGE,"E156.MirrorCS"),sQuery(id+"F0.wireOp",EDGE,"E158.MirrorCS"),sQuery(id+"F0.wireOp",EDGE,"E161.MirrorCS"),sQuery(id+"F0.wireOp",EDGE,"E162.MirrorCS")])]}),"instanceName":"1"}),"instanceName":"1"}),"instanceName":"2"})});
            var Q1;
            Q1=makeQuery(id+"F10.boolean.opBoolean","SPLIT",BODY,{"disambiguationData":[OD(0.0)],"derivedFrom":makeQuery(id+"F7.opPattern","COPY",BODY,{"derivedFrom":makeQuery(id+"F3.opPattern","COPY",BODY,{"derivedFrom":makeQuery(id+"F1.opExtrude","SWEPT_BODY",BODY,{"disambiguationData":[OSD([sQuery(id+"F0.wireOp",EDGE,"E0"),sQuery(id+"F0.wireOp",EDGE,"E1"),sQuery(id+"F0.wireOp",EDGE,"E4.filletArc"),sQuery(id+"F0.wireOp",EDGE,"E5.bottom"),sQuery(id+"F0.wireOp",EDGE,"E5.top"),sQuery(id+"F0.wireOp",EDGE,"E5.left"),sQuery(id+"F0.wireOp",EDGE,"E5.right"),sQuery(id+"F0.wireOp",EDGE,"E6"),sQuery(id+"F0.wireOp",EDGE,"E7"),sQuery(id+"F0.wireOp",EDGE,"E8"),sQuery(id+"F0.wireOp",EDGE,"E9"),sQuery(id+"F0.wireOp",EDGE,"E10"),sQuery(id+"F0.wireOp",EDGE,"E11"),sQuery(id+"F0.wireOp",EDGE,"E12"),sQuery(id+"F0.wireOp",EDGE,"E13"),sQuery(id+"F0.wireOp",EDGE,"E15"),sQuery(id+"F0.wireOp",EDGE,"E16"),sQuery(id+"F0.wireOp",EDGE,"E17"),sQuery(id+"F0.wireOp",EDGE,"E18.filletArc"),sQuery(id+"F0.wireOp",EDGE,"E19.filletArc"),sQuery(id+"F0.wireOp",EDGE,"E20.filletArc"),sQuery(id+"F0.wireOp",EDGE,"E21.filletArc"),sQuery(id+"F0.wireOp",EDGE,"E22.filletArc"),sQuery(id+"F0.wireOp",EDGE,"E23.filletArc"),sQuery(id+"F0.wireOp",EDGE,"E24.MirrorCS"),sQuery(id+"F0.wireOp",EDGE,"E25.MirrorCS"),sQuery(id+"F0.wireOp",EDGE,"E26.MirrorCS"),sQuery(id+"F0.wireOp",EDGE,"E27.MirrorCS"),sQuery(id+"F0.wireOp",EDGE,"E28.MirrorCS"),sQuery(id+"F0.wireOp",EDGE,"E29.MirrorCS"),sQuery(id+"F0.wireOp",EDGE,"E30.MirrorCS"),sQuery(id+"F0.wireOp",EDGE,"E31.MirrorCS"),sQuery(id+"F0.wireOp",EDGE,"E32.MirrorCS"),sQuery(id+"F0.wireOp",EDGE,"E33.MirrorCS"),sQuery(id+"F0.wireOp",EDGE,"E34.MirrorCS"),sQuery(id+"F0.wireOp",EDGE,"E35.MirrorCS"),sQuery(id+"F0.wireOp",EDGE,"E36.MirrorCS"),sQuery(id+"F0.wireOp",EDGE,"E37.MirrorCS"),sQuery(id+"F0.wireOp",EDGE,"E38.MirrorCS"),sQuery(id+"F0.wireOp",EDGE,"E39.MirrorCS"),sQuery(id+"F0.wireOp",EDGE,"E40.MirrorCS"),sQuery(id+"F0.wireOp",EDGE,"E41.MirrorCS"),sQuery(id+"F0.wireOp",EDGE,"E42.MirrorCS"),sQuery(id+"F0.wireOp",EDGE,"E43.MirrorCS"),sQuery(id+"F0.wireOp",EDGE,"E44.MirrorCS"),sQuery(id+"F0.wireOp",EDGE,"E45.MirrorCS"),sQuery(id+"F0.wireOp",EDGE,"E46.MirrorCS"),sQuery(id+"F0.wireOp",EDGE,"E47.MirrorCS"),sQuery(id+"F0.wireOp",EDGE,"E48.MirrorCS"),sQuery(id+"F0.wireOp",EDGE,"E50.MirrorCS"),sQuery(id+"F0.wireOp",EDGE,"E51.MirrorCS"),sQuery(id+"F0.wireOp",EDGE,"E52.MirrorCS"),sQuery(id+"F0.wireOp",EDGE,"E53.MirrorCS"),sQuery(id+"F0.wireOp",EDGE,"E54.MirrorCS"),sQuery(id+"F0.wireOp",EDGE,"E59.MirrorCS"),sQuery(id+"F0.wireOp",EDGE,"E60.MirrorCS"),sQuery(id+"F0.wireOp",EDGE,"E61.MirrorCS"),sQuery(id+"F0.wireOp",EDGE,"E62.MirrorCS"),sQuery(id+"F0.wireOp",EDGE,"E63.MirrorCS"),sQuery(id+"F0.wireOp",EDGE,"E64.MirrorCS"),sQuery(id+"F0.wireOp",EDGE,"E65.MirrorCS"),sQuery(id+"F0.wireOp",EDGE,"E66.MirrorCS"),sQuery(id+"F0.wireOp",EDGE,"E67.MirrorCS"),sQuery(id+"F0.wireOp",EDGE,"E68.MirrorCS"),sQuery(id+"F0.wireOp",EDGE,"E69.MirrorCS"),sQuery(id+"F0.wireOp",EDGE,"E71.MirrorCS"),sQuery(id+"F0.wireOp",EDGE,"E73.MirrorCS"),sQuery(id+"F0.wireOp",EDGE,"E74.MirrorCS"),sQuery(id+"F0.wireOp",EDGE,"E75.MirrorCS"),sQuery(id+"F0.wireOp",EDGE,"E76.MirrorCS"),sQuery(id+"F0.wireOp",EDGE,"E77.MirrorCS"),sQuery(id+"F0.wireOp",EDGE,"E79.MirrorCS"),sQuery(id+"F0.wireOp",EDGE,"E80.MirrorCS"),sQuery(id+"F0.wireOp",EDGE,"E81.MirrorCS"),sQuery(id+"F0.wireOp",EDGE,"E82.MirrorCS"),sQuery(id+"F0.wireOp",EDGE,"E83.MirrorCS"),sQuery(id+"F0.wireOp",EDGE,"E84.MirrorCS"),sQuery(id+"F0.wireOp",EDGE,"E85.MirrorCS"),sQuery(id+"F0.wireOp",EDGE,"E86.MirrorCS"),sQuery(id+"F0.wireOp",EDGE,"E87.MirrorCS"),sQuery(id+"F0.wireOp",EDGE,"E88.MirrorCS"),sQuery(id+"F0.wireOp",EDGE,"E89.MirrorCS"),sQuery(id+"F0.wireOp",EDGE,"E90.MirrorCS"),sQuery(id+"F0.wireOp",EDGE,"E91.MirrorCS"),sQuery(id+"F0.wireOp",EDGE,"E92.MirrorCS"),sQuery(id+"F0.wireOp",EDGE,"E93.MirrorCS"),sQuery(id+"F0.wireOp",EDGE,"E94.MirrorCS"),sQuery(id+"F0.wireOp",EDGE,"E95.MirrorCS"),sQuery(id+"F0.wireOp",EDGE,"E96.MirrorCS"),sQuery(id+"F0.wireOp",EDGE,"E97.MirrorCS"),sQuery(id+"F0.wireOp",EDGE,"E98.MirrorCS"),sQuery(id+"F0.wireOp",EDGE,"E99.MirrorCS"),sQuery(id+"F0.wireOp",EDGE,"E100.MirrorCS"),sQuery(id+"F0.wireOp",EDGE,"E101.MirrorCS"),sQuery(id+"F0.wireOp",EDGE,"E102.MirrorCS"),sQuery(id+"F0.wireOp",EDGE,"E103.MirrorCS"),sQuery(id+"F0.wireOp",EDGE,"E104.MirrorCS"),sQuery(id+"F0.wireOp",EDGE,"E105.MirrorCS"),sQuery(id+"F0.wireOp",EDGE,"E106.MirrorCS"),sQuery(id+"F0.wireOp",EDGE,"E107.MirrorCS"),sQuery(id+"F0.wireOp",EDGE,"E108.MirrorCS"),sQuery(id+"F0.wireOp",EDGE,"E109.MirrorCS"),sQuery(id+"F0.wireOp",EDGE,"E110.MirrorCS"),sQuery(id+"F0.wireOp",EDGE,"E111.MirrorCS"),sQuery(id+"F0.wireOp",EDGE,"E112.MirrorCS"),sQuery(id+"F0.wireOp",EDGE,"E113.MirrorCS"),sQuery(id+"F0.wireOp",EDGE,"E114.MirrorCS"),sQuery(id+"F0.wireOp",EDGE,"E119.MirrorCS"),sQuery(id+"F0.wireOp",EDGE,"E120.MirrorCS"),sQuery(id+"F0.wireOp",EDGE,"E121.MirrorCS"),sQuery(id+"F0.wireOp",EDGE,"E125.MirrorCS"),sQuery(id+"F0.wireOp",EDGE,"E126.MirrorCS"),sQuery(id+"F0.wireOp",EDGE,"E127.MirrorCS"),sQuery(id+"F0.wireOp",EDGE,"E128.MirrorCS"),sQuery(id+"F0.wireOp",EDGE,"E129.MirrorCS"),sQuery(id+"F0.wireOp",EDGE,"E130.MirrorCS"),sQuery(id+"F0.wireOp",EDGE,"E131.MirrorCS"),sQuery(id+"F0.wireOp",EDGE,"E132.MirrorCS"),sQuery(id+"F0.wireOp",EDGE,"E133.MirrorCS"),sQuery(id+"F0.wireOp",EDGE,"E134.MirrorCS"),sQuery(id+"F0.wireOp",EDGE,"E135.MirrorCS"),sQuery(id+"F0.wireOp",EDGE,"E136.MirrorCS"),sQuery(id+"F0.wireOp",EDGE,"E137.MirrorCS"),sQuery(id+"F0.wireOp",EDGE,"E138.MirrorCS"),sQuery(id+"F0.wireOp",EDGE,"E139.MirrorCS"),sQuery(id+"F0.wireOp",EDGE,"E140.MirrorCS"),sQuery(id+"F0.wireOp",EDGE,"E141.MirrorCS"),sQuery(id+"F0.wireOp",EDGE,"E142.MirrorCS"),sQuery(id+"F0.wireOp",EDGE,"E143.MirrorCS"),sQuery(id+"F0.wireOp",EDGE,"E145.MirrorCS"),sQuery(id+"F0.wireOp",EDGE,"E146.MirrorCS"),sQuery(id+"F0.wireOp",EDGE,"E148.MirrorCS"),sQuery(id+"F0.wireOp",EDGE,"E150.MirrorCS"),sQuery(id+"F0.wireOp",EDGE,"E152.MirrorCS"),sQuery(id+"F0.wireOp",EDGE,"E153.MirrorCS"),sQuery(id+"F0.wireOp",EDGE,"E154.MirrorCS"),sQuery(id+"F0.wireOp",EDGE,"E155.MirrorCS"),sQuery(id+"F0.wireOp",EDGE,"E156.MirrorCS"),sQuery(id+"F0.wireOp",EDGE,"E158.MirrorCS"),sQuery(id+"F0.wireOp",EDGE,"E161.MirrorCS"),sQuery(id+"F0.wireOp",EDGE,"E162.MirrorCS")])]}),"instanceName":"1"}),"instanceName":"2"})});
            deleteBodies(context, id + "F12", {"entities" : qUnion([Q0, Q1])});
        }
    });
